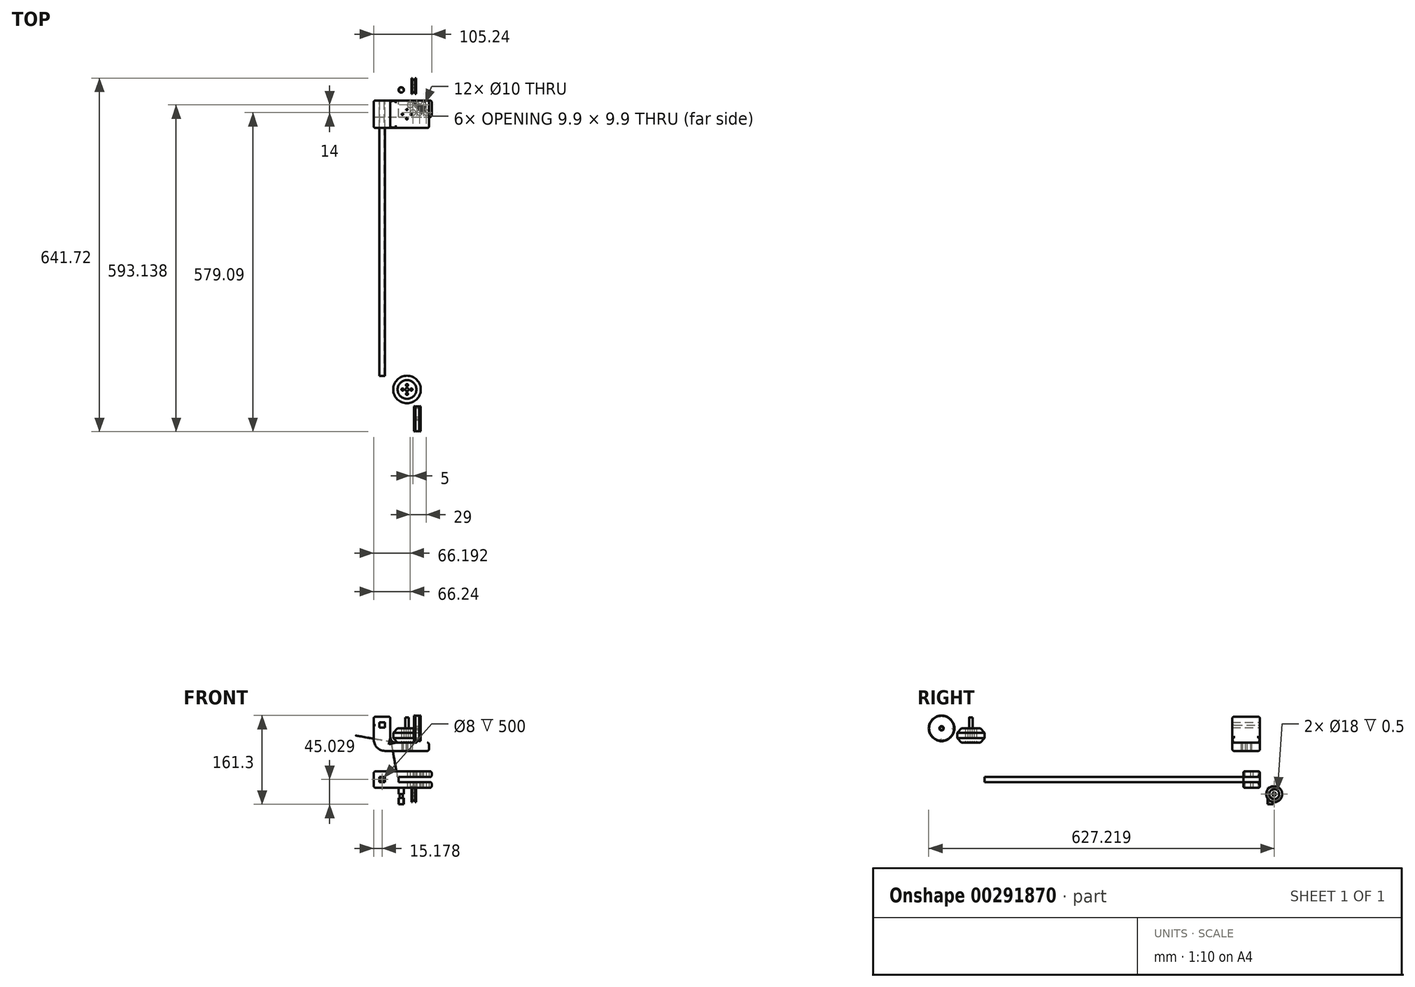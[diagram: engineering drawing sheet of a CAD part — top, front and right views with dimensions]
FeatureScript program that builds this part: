
annotation { "Feature Type Name" : "Feature", "Feature Type Description" : "" }
export const myFeature = defineFeature(function(context is Context, id is Id, definition is map)
    precondition{}
    {
        {
            var Q0;
            Q0=qCreatedBy(makeId("Front.planeOp"),FACE);
            var sketch = newSketch(context, id + "F0", { "sketchPlane" : qUnion([Q0])});
            skLineSegment(sketch, "E0.bottom", {"start": v(0, 0) * mm, "end": v(10, 0) * mm});
            skLineSegment(sketch, "E0.top", {"start": v(0, 10) * mm, "end": v(10, 10) * mm});
            skLineSegment(sketch, "E0.left", {"start": v(0, 0) * mm, "end": v(0, 10) * mm});
            skLineSegment(sketch, "E0.right", {"start": v(10, 0) * mm, "end": v(10, 10) * mm});
            skCircle(sketch, "E1", {"center": v(4.94, 5.03) * mm, "radius": 4 * mm});
            skSolve(sketch);
        }
        {
            var Q0;
            Q0=makeQuery(id+"F0.imprint","IMPRINT",FACE,{"disambiguationData":[TD([[makeQuery(id+"F0.imprint","IMPRINT",EDGE,{"derivedFrom":sQuery(id+"F0.wireOp",EDGE,"E0.bottom")}),1.0]])]});
            extrude(context, id + "F1", {"entities" : qUnion([Q0]), "depth" : 500 * mm});
        }
        {
            var Q0;
            Q0=makeQuery(id+"F0.imprint","IMPRINT",FACE,{"disambiguationData":[TD([[makeQuery(id+"F0.imprint","IMPRINT",EDGE,{"derivedFrom":sQuery(id+"F0.wireOp",EDGE,"E0.bottom")}),1.0]])]});
            var sketch = newSketch(context, id + "F2", { "sketchPlane" : qUnion([Q0])});
            skLineSegment(sketch, "E2.bottom", {"start": v(0, 0) * mm, "end": v(10, 0) * mm});
            skLineSegment(sketch, "E2.top", {"start": v(0, 10) * mm, "end": v(10, 10) * mm});
            skLineSegment(sketch, "E2.left", {"start": v(0, 0) * mm, "end": v(0, 10) * mm});
            skLineSegment(sketch, "E2.right", {"start": v(10, 0) * mm, "end": v(10, 10) * mm});
            skLineSegment(sketch, "E3.bottom", {"start": v(-10, -10) * mm, "end": v(95, -10) * mm});
            skLineSegment(sketch, "E3.top", {"start": v(-10, 20) * mm, "end": v(95, 20) * mm});
            skLineSegment(sketch, "E3.left", {"start": v(-10, -10) * mm, "end": v(-10, 20) * mm});
            skLineSegment(sketch, "E3.right", {"start": v(95, -10) * mm, "end": v(95, 20) * mm});
            skSolve(sketch);
        }
        {
            var Q0;
            Q0=makeQuery(id+"F2.imprint","IMPRINT",FACE,{"disambiguationData":[TD([[makeQuery(id+"F2.imprint","IMPRINT",EDGE,{"derivedFrom":sQuery(id+"F2.wireOp",EDGE,"E2.bottom")}),-1.0]])]});
            extrude(context, id + "F3", {"entities" : qUnion([Q0]), "depth" : 30 * mm});
        }
        {
            var Q0;
            Q0=makeQuery(id+"F3.opExtrude","SWEPT_FACE",FACE,{"disambiguationData":[OSD([sQuery(id+"F2.wireOp",EDGE,"E3.right")])]});
            var sketch = newSketch(context, id + "F4", { "sketchPlane" : qUnion([Q0])});
            skLineSegment(sketch, "E4.bottom", {"start": v(-30, 0.5) * mm, "end": v(0, 0.5) * mm});
            skLineSegment(sketch, "E4.top", {"start": v(-30, 9.5) * mm, "end": v(0, 9.5) * mm});
            skLineSegment(sketch, "E4.left", {"start": v(-30, 0.5) * mm, "end": v(-30, 9.5) * mm});
            skLineSegment(sketch, "E4.right", {"start": v(0, 0.5) * mm, "end": v(0, 9.5) * mm});
            skSolve(sketch);
        }
        {
            var Q0;
            Q0=makeQuery(id+"F4.imprint","IMPRINT",FACE,{"disambiguationData":[TD([[makeQuery(id+"F4.imprint","IMPRINT",EDGE,{"derivedFrom":sQuery(id+"F4.wireOp",EDGE,"E4.bottom")}),1.0]])]});
            extrude(context, id + "F5", {"entities" : qUnion([Q0]), "operationType" : NewBodyOperationType.REMOVE, "oppositeDirection" : true, "depth" : 60 * mm});
        }
        {
            var Q0;
            Q0=makeQuery(id+"F3.opExtrude","SWEPT_FACE",FACE,{"disambiguationData":[OSD([sQuery(id+"F2.wireOp",EDGE,"E3.bottom")])]});
            var sketch = newSketch(context, id + "F6", { "sketchPlane" : qUnion([Q0])});
            skCircle(sketch, "E5", {"center": v(85, 22) * mm, "radius": 5 * mm});
            skCircle(sketch, "E6", {"center": v(80, 8) * mm, "radius": 5 * mm});
            skCircle(sketch, "E7.1.0.0", {"center": v(73, 22) * mm, "radius": 5 * mm});
            skCircle(sketch, "E7.1.0.1", {"center": v(68, 8) * mm, "radius": 5 * mm});
            skCircle(sketch, "E7.2.0.0", {"center": v(61, 22) * mm, "radius": 5 * mm});
            skCircle(sketch, "E7.2.0.1", {"center": v(56, 8) * mm, "radius": 5 * mm});
            skCircle(sketch, "E7.3.0.0", {"center": v(49, 22) * mm, "radius": 5 * mm});
            skCircle(sketch, "E7.3.0.1", {"center": v(44, 8) * mm, "radius": 5 * mm});
            skLineSegment(sketch, "E7.direction1", {"start": v(80, 8) * mm, "end": v(68, 8) * mm, "construction": true});
            skCircle(sketch, "E8.3.0.1", {"center": v(39.68, -19.2) * mm, "radius": 2.95 * mm});
            skSolve(sketch);
        }
        {
            var Q0;
            Q0=makeQuery(id+"F3.opExtrude","CAP_EDGE",EDGE,{"disambiguationData":[OSD([sQuery(id+"F2.wireOp",EDGE,"E3.top")])],"isStart":false});
            var Q1;
            Q1=makeQuery(id+"F3.opExtrude","SWEPT_EDGE",EDGE,{"disambiguationData":[OSD([sQuery(id+"F2.wireOp",EDGE,"E3.top"),sQuery(id+"F2.wireOp",EDGE,"E3.left")])]});
            var Q2;
            Q2=makeQuery(id+"F3.opExtrude","CAP_EDGE",EDGE,{"disambiguationData":[OSD([sQuery(id+"F2.wireOp",EDGE,"E3.top")])],"isStart":true});
            var Q3;
            {var subQ0=sQuery(id+"F2.wireOp",EDGE,"E3.right");var subQ2=sQuery(id+"F2.wireOp",EDGE,"E3.top");Q3=makeQuery(id+"F5.boolean.opBoolean","SPLIT",FACE,{"disambiguationData":[TD([makeQuery(id+"F3.opExtrude","SWEPT_FACE",FACE,{"disambiguationData":[OSD([subQ2])]})])],"derivedFrom":makeQuery(id+"F3.opExtrude","SWEPT_FACE",FACE,{"disambiguationData":[OSD([subQ0])]})});}
            var Q4;
            Q4=makeQuery(id+"F3.opExtrude","SWEPT_EDGE",EDGE,{"disambiguationData":[OSD([sQuery(id+"F2.wireOp",EDGE,"E3.bottom"),sQuery(id+"F2.wireOp",EDGE,"E3.right")])]});
            var Q5;
            Q5=makeQuery(id+"F5.boolean.opBoolean","COPY",EDGE,{"derivedFrom":makeQuery(id+"F5.opExtrude","CAP_EDGE",EDGE,{"disambiguationData":[OSD([sQuery(id+"F4.wireOp",EDGE,"E4.bottom")])],"isStart":true})});
            var Q6;
            Q6=makeQuery(id+"F5.boolean.opBoolean","COPY",EDGE,{"derivedFrom":makeQuery(id+"F5.opExtrude","SWEPT_EDGE",EDGE,{"disambiguationData":[OSD([sQuery(id+"F2.wireOp",EDGE,"E3.right"),sQuery(id+"F4.wireOp",EDGE,"E4.bottom"),sQuery(id+"F4.wireOp",EDGE,"E4.left")])]})});
            var Q7;
            Q7=makeQuery(id+"F3.opExtrude","CAP_EDGE",EDGE,{"disambiguationData":[OSD([sQuery(id+"F2.wireOp",EDGE,"E3.bottom")])],"isStart":false});
            var Q8;
            Q8=makeQuery(id+"F3.opExtrude","CAP_EDGE",EDGE,{"disambiguationData":[OSD([sQuery(id+"F2.wireOp",EDGE,"E3.left")])],"isStart":false});
            var Q9;
            Q9=makeQuery(id+"F3.opExtrude","SWEPT_EDGE",EDGE,{"disambiguationData":[OSD([sQuery(id+"F2.wireOp",EDGE,"E3.bottom"),sQuery(id+"F2.wireOp",EDGE,"E3.left")])]});
            var Q10;
            Q10=makeQuery(id+"F3.opExtrude","CAP_EDGE",EDGE,{"disambiguationData":[OSD([sQuery(id+"F2.wireOp",EDGE,"E3.left")])],"isStart":true});
            var Q11;
            Q11=makeQuery(id+"F5.boolean.opBoolean","COPY",EDGE,{"derivedFrom":makeQuery(id+"F5.opExtrude","SWEPT_EDGE",EDGE,{"disambiguationData":[OSD([sQuery(id+"F2.wireOp",EDGE,"E3.right"),sQuery(id+"F4.wireOp",EDGE,"E4.bottom"),sQuery(id+"F4.wireOp",EDGE,"E4.right")])]})});
            var Q12;
            Q12=makeQuery(id+"F5.boolean.opBoolean","COPY",EDGE,{"derivedFrom":makeQuery(id+"F5.opExtrude","CAP_EDGE",EDGE,{"disambiguationData":[OSD([sQuery(id+"F4.wireOp",EDGE,"E4.right")])],"isStart":false})});
            var Q13;
            Q13=makeQuery(id+"F5.boolean.opBoolean","COPY",EDGE,{"derivedFrom":makeQuery(id+"F5.opExtrude","SWEPT_EDGE",EDGE,{"disambiguationData":[OSD([sQuery(id+"F2.wireOp",EDGE,"E3.right"),sQuery(id+"F4.wireOp",EDGE,"E4.top"),sQuery(id+"F4.wireOp",EDGE,"E4.right")])]})});
            var Q14;
            Q14=makeQuery(id+"F5.boolean.opBoolean","COPY",EDGE,{"derivedFrom":makeQuery(id+"F5.opExtrude","CAP_EDGE",EDGE,{"disambiguationData":[OSD([sQuery(id+"F4.wireOp",EDGE,"E4.left")])],"isStart":false})});
            var Q15;
            Q15=makeQuery(id+"F5.boolean.opBoolean","COPY",EDGE,{"derivedFrom":makeQuery(id+"F5.opExtrude","SWEPT_EDGE",EDGE,{"disambiguationData":[OSD([sQuery(id+"F2.wireOp",EDGE,"E3.right"),sQuery(id+"F4.wireOp",EDGE,"E4.top"),sQuery(id+"F4.wireOp",EDGE,"E4.left")])]})});
            var Q16;
            {var subQ0=sQuery(id+"F2.wireOp",EDGE,"E3.right");var subQ1=sQuery(id+"F2.wireOp",EDGE,"E3.bottom");Q16=makeQuery(id+"F5.boolean.opBoolean","SPLIT",EDGE,{"disambiguationData":[TD([makeQuery(id+"F3.opExtrude","SWEPT_FACE",FACE,{"disambiguationData":[OSD([subQ1])]})])],"derivedFrom":makeQuery(id+"F3.opExtrude","CAP_EDGE",EDGE,{"disambiguationData":[OSD([subQ0])],"isStart":false})});}
            var Q17;
            {var subQ0=sQuery(id+"F2.wireOp",EDGE,"E3.right");var subQ1=sQuery(id+"F2.wireOp",EDGE,"E3.bottom");Q17=makeQuery(id+"F5.boolean.opBoolean","SPLIT",EDGE,{"disambiguationData":[TD([makeQuery(id+"F3.opExtrude","SWEPT_FACE",FACE,{"disambiguationData":[OSD([subQ1])]})])],"derivedFrom":makeQuery(id+"F3.opExtrude","CAP_EDGE",EDGE,{"disambiguationData":[OSD([subQ0])],"isStart":true})});}
            var Q18;
            Q18=makeQuery(id+"F3.opExtrude","CAP_EDGE",EDGE,{"disambiguationData":[OSD([sQuery(id+"F2.wireOp",EDGE,"E3.bottom")])],"isStart":true});
            fillet(context, id + "F7", {"entities" : qUnion([Q0, Q1, Q2, Q3, Q4, Q5, Q6, Q7, Q8, Q9, Q10, Q11, Q12, Q13, Q14, Q15, Q16, Q17, Q18]), "radius" : 3 * mm, "tangentPropagation" : true, "allowEdgeOverflow" : false});
        }
        {
            var Q0;
            Q0=makeQuery(id+"F6.imprint","IMPRINT",FACE,{"disambiguationData":[TD([[makeQuery(id+"F6.imprint","IMPRINT",EDGE,{"derivedFrom":sQuery(id+"F6.wireOp",EDGE,"E5")}),1.0]])]});
            var Q1;
            Q1=makeQuery(id+"F6.imprint","IMPRINT",FACE,{"disambiguationData":[TD([[makeQuery(id+"F6.imprint","IMPRINT",EDGE,{"derivedFrom":sQuery(id+"F6.wireOp",EDGE,"E6")}),1.0]])]});
            var Q2;
            Q2=makeQuery(id+"F6.imprint","IMPRINT",FACE,{"disambiguationData":[TD([[makeQuery(id+"F6.imprint","IMPRINT",EDGE,{"derivedFrom":sQuery(id+"F6.wireOp",EDGE,"E7.1.0.0")}),1.0]])]});
            var Q3;
            Q3=makeQuery(id+"F6.imprint","IMPRINT",FACE,{"disambiguationData":[TD([[makeQuery(id+"F6.imprint","IMPRINT",EDGE,{"derivedFrom":sQuery(id+"F6.wireOp",EDGE,"E7.1.0.1")}),1.0]])]});
            var Q4;
            Q4=makeQuery(id+"F6.imprint","IMPRINT",FACE,{"disambiguationData":[TD([[makeQuery(id+"F6.imprint","IMPRINT",EDGE,{"derivedFrom":sQuery(id+"F6.wireOp",EDGE,"E7.2.0.0")}),1.0]])]});
            var Q5;
            Q5=makeQuery(id+"F6.imprint","IMPRINT",FACE,{"disambiguationData":[TD([[makeQuery(id+"F6.imprint","IMPRINT",EDGE,{"derivedFrom":sQuery(id+"F6.wireOp",EDGE,"E7.2.0.1")}),1.0]])]});
            var Q6;
            Q6=sQuery(id+"F6.wireOp",EDGE,"E5");
            var Q7;
            Q7=sQuery(id+"F6.wireOp",EDGE,"E6");
            var Q8;
            Q8=sQuery(id+"F6.wireOp",EDGE,"E7.1.0.1");
            var Q9;
            Q9=sQuery(id+"F6.wireOp",EDGE,"E7.1.0.0");
            var Q10;
            Q10=sQuery(id+"F6.wireOp",EDGE,"E7.2.0.0");
            extrude(context, id + "F8", {"entities" : qUnion([Q0, Q1, Q2, Q3, Q4, Q5]), "operationType" : NewBodyOperationType.REMOVE, "surfaceEntities" : qUnion([Q6, Q7, Q8, Q9, Q10]), "oppositeDirection" : true, "depth" : 30 * mm});
        }
        {
            var Q0;
            Q0=makeQuery(id+"F6.imprint","IMPRINT",FACE,{"disambiguationData":[TD([[makeQuery(id+"F6.imprint","IMPRINT",EDGE,{"derivedFrom":sQuery(id+"F6.wireOp",EDGE,"E8.3.0.1")}),1.0]])]});
            extrude(context, id + "F9", {"entities" : qUnion([Q0]), "depth" : 30 * mm});
        }
        {
            var Q0;
            Q0=makeQuery(id+"F9.opExtrude","CAP_FACE",FACE,{"disambiguationData":[OSD([sQuery(id+"F6.wireOp",EDGE,"E8.3.0.1")])],"isStart":false});
            var sketch = newSketch(context, id + "F10", { "sketchPlane" : qUnion([Q0])});
            skCircle(sketch, "E9", {"center": v(39.68, -19.2) * mm, "radius": 4.95 * mm});
            skSolve(sketch);
        }
        {
            var Q0;
            Q0=makeQuery(id+"F6.imprint","IMPRINT",FACE,{"disambiguationData":[TD([[makeQuery(id+"F6.imprint","IMPRINT",EDGE,{"derivedFrom":sQuery(id+"F6.wireOp",EDGE,"E8.3.0.1")}),1.0]])]});
            var sketch = newSketch(context, id + "F11", { "sketchPlane" : qUnion([Q0])});
            skCircle(sketch, "E10", {"center": v(39.69, -19.21) * mm, "radius": 4.9 * mm});
            skSolve(sketch);
        }
        {
            var Q0;
            Q0=makeQuery(id+"F11.imprint","IMPRINT",FACE,{"disambiguationData":[TD([[makeQuery(id+"F11.imprint","IMPRINT",EDGE,{"derivedFrom":sQuery(id+"F11.wireOp",EDGE,"E10")}),1.0]])]});
            extrude(context, id + "F12", {"entities" : qUnion([Q0]), "operationType" : NewBodyOperationType.ADD, "depth" : 11.5 * mm});
        }
        {
            var Q0;
            Q0=makeQuery(id+"F10.imprint","IMPRINT",FACE,{"disambiguationData":[TD([[makeQuery(id+"F10.imprint","IMPRINT",EDGE,{"derivedFrom":sQuery(id+"F10.wireOp",EDGE,"E9")}),1.0]])]});
            extrude(context, id + "F13", {"entities" : qUnion([Q0]), "oppositeDirection" : true, "depth" : 11.5 * mm});
        }
        {
            var Q0;
            Q0=qCreatedBy(makeId("Front.planeOp"),FACE);
            var sketch = newSketch(context, id + "F14", { "sketchPlane" : qUnion([Q0])});
            skPoint(sketch, "E11.firstSnap0", {"position": v(10, 5) * mm});
            skLineSegment(sketch, "E11.bottom", {"start": v(10, 109) * mm, "end": v(0, 109) * mm});
            skLineSegment(sketch, "E11.top", {"start": v(10, 99) * mm, "end": v(0, 99) * mm});
            skLineSegment(sketch, "E11.left", {"start": v(10, 109) * mm, "end": v(10, 99) * mm});
            skLineSegment(sketch, "E11.right", {"start": v(0, 109) * mm, "end": v(0, 104) * mm});
            skLineSegment(sketch, "E12", {"start": v(-10, 57) * mm, "end": v(90, 57) * mm});
            skLineSegment(sketch, "E13", {"start": v(90, 57) * mm, "end": v(90, 104) * mm});
            skLineSegment(sketch, "E14", {"start": v(90, 104) * mm, "end": v(-25.5, 104) * mm});
            skPoint(sketch, "E14.endSnap0", {"position": v(0, 104) * mm});
            skLineSegment(sketch, "E15", {"start": v(-10, 57) * mm, "end": v(-10, 104) * mm});
            skLineSegment(sketch, "E16", {"start": v(0, 99) * mm, "end": v(0, 104) * mm});
            skLineSegment(sketch, "E17", {"start": v(90, 72) * mm, "end": v(-10, 72) * mm});
            skLineSegment(sketch, "E18", {"start": v(20, 104) * mm, "end": v(20, 72) * mm});
            skLineSegment(sketch, "E19", {"start": v(20, 104) * mm, "end": v(20, 119) * mm});
            skLineSegment(sketch, "E20", {"start": v(20, 119) * mm, "end": v(-10.3, 119) * mm});
            skLineSegment(sketch, "E21", {"start": v(-10.3, 119) * mm, "end": v(-10, 104) * mm});
            skSolve(sketch);
        }
        {
            var Q0;
            {var subQ6=sQuery(id+"F14.wireOp",EDGE,"E11.bottom");Q0=makeQuery(id+"F14.imprint","IMPRINT",FACE,{"disambiguationData":[TD([[makeQuery(id+"F14.imprint","IMPRINT",EDGE,{"derivedFrom":subQ6}),-1.0]])]});}
            var Q1;
            {var subQ4=sQuery(id+"F14.wireOp",EDGE,"E11.top");Q1=makeQuery(id+"F14.imprint","IMPRINT",FACE,{"disambiguationData":[TD([[makeQuery(id+"F14.imprint","IMPRINT",EDGE,{"derivedFrom":subQ4}),1.0]])]});}
            var Q2;
            {var subQ1=sQuery(id+"F14.wireOp",EDGE,"E12");Q2=makeQuery(id+"F14.imprint","IMPRINT",FACE,{"disambiguationData":[TD([[makeQuery(id+"F14.imprint","IMPRINT",EDGE,{"derivedFrom":subQ1}),1.0]])]});}
            extrude(context, id + "F15", {"entities" : qUnion([Q0, Q1, Q2]), "depth" : 50 * mm});
        }
        {
            var Q0;
            Q0=makeQuery(id+"F15.opExtrude","SWEPT_EDGE",EDGE,{"disambiguationData":[OSD([sQuery(id+"F14.wireOp",EDGE,"E12"),sQuery(id+"F14.wireOp",EDGE,"E15")])]});
            fillet(context, id + "F16", {"entities" : qUnion([Q0]), "radius" : 20 * mm, "tangentPropagation" : true, "allowEdgeOverflow" : false});
        }
        {
            var Q0;
            Q0=makeQuery(id+"F15.opExtrude","SWEPT_FACE",FACE,{"disambiguationData":[OSD([sQuery(id+"F14.wireOp",EDGE,"E12")])]});
            var sketch = newSketch(context, id + "F17", { "sketchPlane" : qUnion([Q0])});
            skCircle(sketch, "E22", {"center": v(58, 25) * mm, "radius": 1.5 * mm});
            skCircle(sketch, "E23", {"center": v(42, 25) * mm, "radius": 1.5 * mm});
            skCircle(sketch, "E24", {"center": v(50, 33) * mm, "radius": 1.5 * mm});
            skCircle(sketch, "E25", {"center": v(50, 17) * mm, "radius": 1.5 * mm});
            skLineSegment(sketch, "E26", {"start": v(50, 33) * mm, "end": v(50, 17) * mm});
            skLineSegment(sketch, "E27", {"start": v(42, 25) * mm, "end": v(58, 25) * mm});
            skPoint(sketch, "E28", {"position": v(50, 25) * mm});
            skCircle(sketch, "E29", {"center": v(50, 25) * mm, "radius": 8 * mm});
            skLineSegment(sketch, "E30", {"start": v(58, 25) * mm, "end": v(42, 25) * mm});
            skLineSegment(sketch, "E31", {"start": v(50, 50) * mm, "end": v(50, 0) * mm});
            skPoint(sketch, "E31.endSnap0", {"position": v(50, 0) * mm});
            skSolve(sketch);
        }
        {
            var Q0;
            {var subQ0=sQuery(id+"F17.wireOp",EDGE,"E31");var subQ1=sQuery(id+"F17.wireOp",EDGE,"E24");var subQ2=makeQuery(id+"F17.imprint","INTERSECT",VERTEX,{"disambiguationData":[OD(0.0)],"derivedFrom":[subQ1,subQ0]});Q0=makeQuery(id+"F17.imprint","IMPRINT",FACE,{"disambiguationData":[TD([[makeQuery(id+"F17.imprint","IMPRINT",EDGE,{"disambiguationData":[TD([[subQ2,1.0]])],"derivedFrom":subQ1}),1.0]])]});}
            var Q1;
            {var subQ0=sQuery(id+"F17.wireOp",EDGE,"E31");var subQ1=sQuery(id+"F17.wireOp",EDGE,"E24");var subQ2=makeQuery(id+"F17.imprint","INTERSECT",VERTEX,{"disambiguationData":[OD(1.0)],"derivedFrom":[subQ1,subQ0]});Q1=makeQuery(id+"F17.imprint","IMPRINT",FACE,{"disambiguationData":[TD([[makeQuery(id+"F17.imprint","IMPRINT",EDGE,{"disambiguationData":[TD([[subQ2,-1.0]])],"derivedFrom":subQ1}),1.0]])]});}
            var Q2;
            {var subQ0=sQuery(id+"F17.wireOp",EDGE,"E29");var subQ1=sQuery(id+"F17.wireOp",EDGE,"E24");var subQ2=makeQuery(id+"F17.imprint","INTERSECT",VERTEX,{"disambiguationData":[OD(0.0)],"derivedFrom":[subQ1,subQ0]});Q2=makeQuery(id+"F17.imprint","IMPRINT",FACE,{"disambiguationData":[TD([[makeQuery(id+"F17.imprint","IMPRINT",EDGE,{"disambiguationData":[TD([[subQ2,-1.0]])],"derivedFrom":subQ1}),1.0]])]});}
            var Q3;
            {var subQ0=sQuery(id+"F17.wireOp",EDGE,"E29");var subQ1=sQuery(id+"F17.wireOp",EDGE,"E24");var subQ2=makeQuery(id+"F17.imprint","INTERSECT",VERTEX,{"disambiguationData":[OD(0.0)],"derivedFrom":[subQ1,subQ0]});Q3=makeQuery(id+"F17.imprint","IMPRINT",FACE,{"disambiguationData":[TD([[makeQuery(id+"F17.imprint","IMPRINT",EDGE,{"disambiguationData":[TD([[subQ2,1.0]])],"derivedFrom":subQ1}),1.0]])]});}
            var Q4;
            {var subQ0=sQuery(id+"F17.wireOp",EDGE,"E29");var subQ1=sQuery(id+"F17.wireOp",EDGE,"E23");var subQ2=makeQuery(id+"F17.imprint","INTERSECT",VERTEX,{"disambiguationData":[OD(0.0)],"derivedFrom":[subQ1,subQ0]});Q4=makeQuery(id+"F17.imprint","IMPRINT",FACE,{"disambiguationData":[TD([[makeQuery(id+"F17.imprint","IMPRINT",EDGE,{"disambiguationData":[TD([[subQ2,1.0]])],"derivedFrom":subQ1}),1.0]])]});}
            var Q5;
            {var subQ0=sQuery(id+"F17.wireOp",EDGE,"E30");var subQ1=sQuery(id+"F17.wireOp",EDGE,"E23");var subQ2=makeQuery(id+"F17.imprint","INTERSECT",VERTEX,{"derivedFrom":[subQ1,subQ0]});Q5=makeQuery(id+"F17.imprint","IMPRINT",FACE,{"disambiguationData":[TD([[makeQuery(id+"F17.imprint","IMPRINT",EDGE,{"disambiguationData":[TD([[subQ2,1.0]])],"derivedFrom":subQ1}),1.0]])]});}
            var Q6;
            {var subQ0=sQuery(id+"F17.wireOp",EDGE,"E29");var subQ1=sQuery(id+"F17.wireOp",EDGE,"E23");var subQ2=makeQuery(id+"F17.imprint","INTERSECT",VERTEX,{"disambiguationData":[OD(0.0)],"derivedFrom":[subQ1,subQ0]});Q6=makeQuery(id+"F17.imprint","IMPRINT",FACE,{"disambiguationData":[TD([[makeQuery(id+"F17.imprint","IMPRINT",EDGE,{"disambiguationData":[TD([[subQ2,-1.0]])],"derivedFrom":subQ1}),1.0]])]});}
            var Q7;
            {var subQ0=sQuery(id+"F17.wireOp",EDGE,"E29");var subQ1=sQuery(id+"F17.wireOp",EDGE,"E25");var subQ2=makeQuery(id+"F17.imprint","INTERSECT",VERTEX,{"disambiguationData":[OD(0.0)],"derivedFrom":[subQ1,subQ0]});Q7=makeQuery(id+"F17.imprint","IMPRINT",FACE,{"disambiguationData":[TD([[makeQuery(id+"F17.imprint","IMPRINT",EDGE,{"disambiguationData":[TD([[subQ2,1.0]])],"derivedFrom":subQ1}),1.0]])]});}
            var Q8;
            {var subQ0=sQuery(id+"F17.wireOp",EDGE,"E31");var subQ1=sQuery(id+"F17.wireOp",EDGE,"E25");var subQ2=makeQuery(id+"F17.imprint","INTERSECT",VERTEX,{"disambiguationData":[OD(0.0)],"derivedFrom":[subQ1,subQ0]});Q8=makeQuery(id+"F17.imprint","IMPRINT",FACE,{"disambiguationData":[TD([[makeQuery(id+"F17.imprint","IMPRINT",EDGE,{"disambiguationData":[TD([[subQ2,1.0]])],"derivedFrom":subQ1}),1.0]])]});}
            var Q9;
            {var subQ0=sQuery(id+"F17.wireOp",EDGE,"E31");var subQ1=sQuery(id+"F17.wireOp",EDGE,"E25");var subQ2=makeQuery(id+"F17.imprint","INTERSECT",VERTEX,{"disambiguationData":[OD(0.0)],"derivedFrom":[subQ1,subQ0]});Q9=makeQuery(id+"F17.imprint","IMPRINT",FACE,{"disambiguationData":[TD([[makeQuery(id+"F17.imprint","IMPRINT",EDGE,{"disambiguationData":[TD([[subQ2,-1.0]])],"derivedFrom":subQ1}),1.0]])]});}
            var Q10;
            {var subQ0=sQuery(id+"F17.wireOp",EDGE,"E29");var subQ1=sQuery(id+"F17.wireOp",EDGE,"E25");var subQ2=makeQuery(id+"F17.imprint","INTERSECT",VERTEX,{"disambiguationData":[OD(1.0)],"derivedFrom":[subQ1,subQ0]});Q10=makeQuery(id+"F17.imprint","IMPRINT",FACE,{"disambiguationData":[TD([[makeQuery(id+"F17.imprint","IMPRINT",EDGE,{"disambiguationData":[TD([[subQ2,-1.0]])],"derivedFrom":subQ1}),1.0]])]});}
            var Q11;
            {var subQ0=sQuery(id+"F17.wireOp",EDGE,"E30");var subQ1=sQuery(id+"F17.wireOp",EDGE,"E22");var subQ2=makeQuery(id+"F17.imprint","INTERSECT",VERTEX,{"derivedFrom":[subQ1,subQ0]});Q11=makeQuery(id+"F17.imprint","IMPRINT",FACE,{"disambiguationData":[TD([[makeQuery(id+"F17.imprint","IMPRINT",EDGE,{"disambiguationData":[TD([[subQ2,1.0]])],"derivedFrom":subQ1}),1.0]])]});}
            var Q12;
            {var subQ0=sQuery(id+"F17.wireOp",EDGE,"E30");var subQ1=sQuery(id+"F17.wireOp",EDGE,"E22");var subQ2=makeQuery(id+"F17.imprint","INTERSECT",VERTEX,{"derivedFrom":[subQ1,subQ0]});Q12=makeQuery(id+"F17.imprint","IMPRINT",FACE,{"disambiguationData":[TD([[makeQuery(id+"F17.imprint","IMPRINT",EDGE,{"disambiguationData":[TD([[subQ2,-1.0]])],"derivedFrom":subQ1}),1.0]])]});}
            var Q13;
            {var subQ0=sQuery(id+"F17.wireOp",EDGE,"E29");var subQ1=sQuery(id+"F17.wireOp",EDGE,"E22");var subQ2=makeQuery(id+"F17.imprint","INTERSECT",VERTEX,{"disambiguationData":[OD(0.0)],"derivedFrom":[subQ1,subQ0]});Q13=makeQuery(id+"F17.imprint","IMPRINT",FACE,{"disambiguationData":[TD([[makeQuery(id+"F17.imprint","IMPRINT",EDGE,{"disambiguationData":[TD([[subQ2,1.0]])],"derivedFrom":subQ1}),1.0]])]});}
            extrude(context, id + "F18", {"entities" : qUnion([Q0, Q1, Q2, Q3, Q4, Q5, Q6, Q7, Q8, Q9, Q10, Q11, Q12, Q13]), "operationType" : NewBodyOperationType.REMOVE, "oppositeDirection" : true, "depth" : 25 * mm});
        }
        {
            var Q0;
            Q0=makeQuery(id+"F15.opExtrude","SWEPT_FACE",FACE,{"disambiguationData":[OSD([sQuery(id+"F14.wireOp",EDGE,"E17")])]});
            var sketch = newSketch(context, id + "F19", { "sketchPlane" : qUnion([Q0])});
            skCircle(sketch, "E32", {"center": v(50.2, -524.51) * mm, "radius": 25 * mm});
            skCircle(sketch, "E33", {"center": v(50.2, -524.51) * mm, "radius": 3 * mm});
            skCircle(sketch, "E34", {"center": v(50.2, -524.51) * mm, "radius": 8 * mm});
            skCircle(sketch, "E35", {"center": v(42.2, -524.51) * mm, "radius": 2 * mm});
            skCircle(sketch, "E36.1.0", {"center": v(50.2, -516.51) * mm, "radius": 2 * mm});
            skCircle(sketch, "E36.2.0", {"center": v(58.2, -524.51) * mm, "radius": 2 * mm});
            skCircle(sketch, "E36.3.0", {"center": v(50.2, -532.51) * mm, "radius": 2 * mm});
            skLineSegment(sketch, "E36.anchor1", {"start": v(50.2, -524.51) * mm, "end": v(42.2, -524.51) * mm, "construction": true});
            skLineSegment(sketch, "E36.anchor2", {"start": v(50.2, -524.51) * mm, "end": v(50.2, -532.51) * mm, "construction": true});
            skSolve(sketch);
        }
        {
            var Q0;
            Q0=makeQuery(id+"F19.imprint","IMPRINT",FACE,{"disambiguationData":[TD([[makeQuery(id+"F19.imprint","IMPRINT",EDGE,{"derivedFrom":sQuery(id+"F19.wireOp",EDGE,"E32")}),1.0]])]});
            extrude(context, id + "F20", {"entities" : qUnion([Q0]), "depth" : 26 * mm});
        }
        {
            var Q0;
            Q0=makeQuery(id+"F20.opExtrude","CAP_EDGE",EDGE,{"disambiguationData":[OSD([sQuery(id+"F19.wireOp",EDGE,"E32")])],"isStart":false});
            var Q1;
            Q1=makeQuery(id+"F20.opExtrude","CAP_EDGE",EDGE,{"disambiguationData":[OSD([sQuery(id+"F19.wireOp",EDGE,"E32")])],"isStart":true});
            chamfer(context, id + "F21", {"entities" : qUnion([Q0, Q1]), "width" : 8 * mm, "tangentPropagation" : true});
        }
        {
            var Q0;
            Q0=makeQuery(id+"F20.opExtrude","CAP_FACE",FACE,{"disambiguationData":[OSD([sQuery(id+"F14.wireOp",EDGE,"E17"),sQuery(id+"F17.wireOp",EDGE,"E22"),sQuery(id+"F17.wireOp",EDGE,"E23"),sQuery(id+"F17.wireOp",EDGE,"E24"),sQuery(id+"F17.wireOp",EDGE,"E25"),sQuery(id+"F19.wireOp",EDGE,"E32"),sQuery(id+"F19.wireOp",EDGE,"E33")])],"isStart":false});
            var sketch = newSketch(context, id + "F22", { "sketchPlane" : qUnion([Q0])});
            skLineSegment(sketch, "E37.bottom", {"start": v(62.8, -602.8) * mm, "end": v(74.8, -602.8) * mm});
            skLineSegment(sketch, "E37.top", {"start": v(62.8, -577.8) * mm, "end": v(74.8, -577.8) * mm});
            skLineSegment(sketch, "E37.left", {"start": v(62.8, -602.8) * mm, "end": v(62.8, -577.8) * mm});
            skLineSegment(sketch, "E37.right", {"start": v(74.8, -602.8) * mm, "end": v(74.8, -577.8) * mm});
            skLineSegment(sketch, "E38", {"start": v(68.8, -602.8) * mm, "end": v(68.8, -577.8) * mm});
            skLineSegment(sketch, "E39", {"start": v(62.8, -602.8) * mm, "end": v(68.8, -596.8) * mm});
            skLineSegment(sketch, "E40", {"start": v(68.8, -596.8) * mm, "end": v(74.8, -602.8) * mm});
            skLineSegment(sketch, "E41", {"start": v(62.8, -580.8) * mm, "end": v(74.8, -580.8) * mm});
            skSolve(sketch);
        }
        {
            var Q0;
            {var subQ0=sQuery(id+"F22.wireOp",EDGE,"E39");Q0=makeQuery(id+"F22.imprint","IMPRINT",FACE,{"disambiguationData":[TD([[makeQuery(id+"F22.imprint","IMPRINT",EDGE,{"derivedFrom":subQ0}),1.0]])]});}
            var Q1;
            {var subQ0=sQuery(id+"F22.wireOp",EDGE,"E40");Q1=makeQuery(id+"F22.imprint","IMPRINT",FACE,{"disambiguationData":[TD([[makeQuery(id+"F22.imprint","IMPRINT",EDGE,{"derivedFrom":subQ0}),1.0]])]});}
            var Q2;
            Q2=sQuery(id+"F22.wireOp",EDGE,"E37.top");
            revolve(context, id + "F23", {"entities" : qUnion([Q0, Q1]), "axis" : qUnion([Q2]), "revolveType" : RevolveType.FULL});
        }
        {
            var Q0;
            Q0=makeQuery(id+"F23.opRevolve","SWEPT_EDGE",EDGE,{"disambiguationData":[OSD([sQuery(id+"F22.wireOp",EDGE,"E38"),sQuery(id+"F22.wireOp",EDGE,"E39"),sQuery(id+"F22.wireOp",EDGE,"E40")])]});
            fillet(context, id + "F24", {"entities" : qUnion([Q0]), "radius" : 1 * mm, "tangentPropagation" : true, "allowEdgeOverflow" : false});
        }
        {
            var Q0;
            Q0=makeQuery(id+"F23.opRevolve","SWEPT_EDGE",EDGE,{"disambiguationData":[OSD([sQuery(id+"F22.wireOp",EDGE,"E37.bottom"),sQuery(id+"F22.wireOp",EDGE,"E37.right"),sQuery(id+"F22.wireOp",EDGE,"E40")])]});
            var Q1;
            Q1=makeQuery(id+"F23.opRevolve","SWEPT_EDGE",EDGE,{"disambiguationData":[OSD([sQuery(id+"F22.wireOp",EDGE,"E37.bottom"),sQuery(id+"F22.wireOp",EDGE,"E37.left"),sQuery(id+"F22.wireOp",EDGE,"E39")])]});
            chamfer(context, id + "F25", {"entities" : qUnion([Q0, Q1]), "width" : 1 * mm, "tangentPropagation" : true});
        }
        {
            var Q0;
            Q0=makeQuery(id+"F23.opRevolve","SWEPT_EDGE",EDGE,{"disambiguationData":[OSD([sQuery(id+"F22.wireOp",EDGE,"E37.right"),sQuery(id+"F22.wireOp",EDGE,"E41")])]});
            var Q1;
            Q1=makeQuery(id+"F23.opRevolve","SWEPT_EDGE",EDGE,{"disambiguationData":[OSD([sQuery(id+"F22.wireOp",EDGE,"E37.left"),sQuery(id+"F22.wireOp",EDGE,"E41")])]});
            chamfer(context, id + "F26", {"entities" : qUnion([Q0, Q1]), "width" : 1 * mm, "tangentPropagation" : true});
        }
        {
            var Q0;
            Q0=makeQuery(id+"F23.opRevolve","SWEPT_FACE",FACE,{"disambiguationData":[OSD([sQuery(id+"F22.wireOp",EDGE,"E37.right")])]});
            var sketch = newSketch(context, id + "F27", { "sketchPlane" : qUnion([Q0])});
            skCircle(sketch, "E42", {"center": v(-577.8, 98) * mm, "radius": 19 * mm});
            skCircle(sketch, "E43", {"center": v(-596.79, 98.55) * mm, "radius": 0.75 * mm});
            skCircle(sketch, "E44.1.0", {"center": v(-596.64, 95.57) * mm, "radius": 0.75 * mm});
            skCircle(sketch, "E44.2.0", {"center": v(-596.03, 92.65) * mm, "radius": 0.75 * mm});
            skCircle(sketch, "E44.3.0", {"center": v(-594.96, 89.87) * mm, "radius": 0.75 * mm});
            skCircle(sketch, "E44.4.0", {"center": v(-593.48, 87.28) * mm, "radius": 0.75 * mm});
            skCircle(sketch, "E44.5.0", {"center": v(-591.6, 84.96) * mm, "radius": 0.75 * mm});
            skCircle(sketch, "E44.6.0", {"center": v(-589.4, 82.96) * mm, "radius": 0.75 * mm});
            skCircle(sketch, "E44.7.0", {"center": v(-586.9, 81.33) * mm, "radius": 0.75 * mm});
            skCircle(sketch, "E44.8.0", {"center": v(-584.18, 80.1) * mm, "radius": 0.75 * mm});
            skCircle(sketch, "E44.9.0", {"center": v(-581.3, 79.33) * mm, "radius": 0.75 * mm});
            skCircle(sketch, "E44.10.0", {"center": v(-578.34, 79.01) * mm, "radius": 0.75 * mm});
            skCircle(sketch, "E44.11.0", {"center": v(-575.36, 79.16) * mm, "radius": 0.75 * mm});
            skCircle(sketch, "E44.12.0", {"center": v(-572.44, 79.77) * mm, "radius": 0.75 * mm});
            skCircle(sketch, "E44.13.0", {"center": v(-569.66, 80.83) * mm, "radius": 0.75 * mm});
            skCircle(sketch, "E44.14.0", {"center": v(-567.07, 82.32) * mm, "radius": 0.75 * mm});
            skCircle(sketch, "E44.15.0", {"center": v(-564.75, 84.19) * mm, "radius": 0.75 * mm});
            skCircle(sketch, "E44.16.0", {"center": v(-562.75, 86.4) * mm, "radius": 0.75 * mm});
            skCircle(sketch, "E44.17.0", {"center": v(-561.12, 88.9) * mm, "radius": 0.75 * mm});
            skCircle(sketch, "E44.18.0", {"center": v(-559.9, 91.61) * mm, "radius": 0.75 * mm});
            skCircle(sketch, "E44.19.0", {"center": v(-559.12, 94.5) * mm, "radius": 0.75 * mm});
            skCircle(sketch, "E45.1.20.0", {"center": v(-558.8, 97.46) * mm, "radius": 0.75 * mm});
            skCircle(sketch, "E45.1.21.0", {"center": v(-558.95, 100.43) * mm, "radius": 0.75 * mm});
            skCircle(sketch, "E45.1.22.0", {"center": v(-559.56, 103.35) * mm, "radius": 0.75 * mm});
            skCircle(sketch, "E45.1.23.0", {"center": v(-560.62, 106.14) * mm, "radius": 0.75 * mm});
            skCircle(sketch, "E45.1.24.0", {"center": v(-562.1, 108.72) * mm, "radius": 0.75 * mm});
            skCircle(sketch, "E45.1.25.0", {"center": v(-563.98, 111.05) * mm, "radius": 0.75 * mm});
            skCircle(sketch, "E45.1.26.0", {"center": v(-566.19, 113.05) * mm, "radius": 0.75 * mm});
            skCircle(sketch, "E45.1.27.0", {"center": v(-568.68, 114.68) * mm, "radius": 0.75 * mm});
            skCircle(sketch, "E45.1.28.0", {"center": v(-571.4, 115.9) * mm, "radius": 0.75 * mm});
            skCircle(sketch, "E45.1.29.0", {"center": v(-574.28, 116.68) * mm, "radius": 0.75 * mm});
            skCircle(sketch, "E46.1.30.0", {"center": v(-577.25, 117) * mm, "radius": 0.75 * mm});
            skCircle(sketch, "E46.1.31.0", {"center": v(-580.23, 116.85) * mm, "radius": 0.75 * mm});
            skCircle(sketch, "E46.1.32.0", {"center": v(-583.14, 116.23) * mm, "radius": 0.75 * mm});
            skCircle(sketch, "E46.1.33.0", {"center": v(-585.93, 115.17) * mm, "radius": 0.75 * mm});
            skCircle(sketch, "E46.1.34.0", {"center": v(-588.52, 113.69) * mm, "radius": 0.75 * mm});
            skCircle(sketch, "E46.1.35.0", {"center": v(-590.84, 111.82) * mm, "radius": 0.75 * mm});
            skCircle(sketch, "E46.1.36.0", {"center": v(-592.84, 109.6) * mm, "radius": 0.75 * mm});
            skCircle(sketch, "E46.1.37.0", {"center": v(-594.47, 107.11) * mm, "radius": 0.75 * mm});
            skCircle(sketch, "E46.1.38.0", {"center": v(-595.69, 104.4) * mm, "radius": 0.75 * mm});
            skCircle(sketch, "E46.1.39.0", {"center": v(-596.47, 101.51) * mm, "radius": 0.75 * mm});
            skSolve(sketch);
        }
        {
            var Q0;
            {var subQ0=sQuery(id+"F27.wireOp",EDGE,"E45.1.21.0");var subQ1=sQuery(id+"F27.wireOp",EDGE,"E42");var subQ2=makeQuery(id+"F27.imprint","INTERSECT",VERTEX,{"disambiguationData":[OD(0.0)],"derivedFrom":[subQ1,subQ0]});Q0=makeQuery(id+"F27.imprint","IMPRINT",FACE,{"disambiguationData":[TD([[makeQuery(id+"F27.imprint","IMPRINT",EDGE,{"disambiguationData":[TD([[subQ2,-1.0]])],"derivedFrom":subQ1}),-1.0]])]});}
            var Q1;
            {var subQ0=sQuery(id+"F27.wireOp",EDGE,"E45.1.21.0");var subQ1=sQuery(id+"F27.wireOp",EDGE,"E42");var subQ2=makeQuery(id+"F27.imprint","INTERSECT",VERTEX,{"disambiguationData":[OD(0.0)],"derivedFrom":[subQ1,subQ0]});Q1=makeQuery(id+"F27.imprint","IMPRINT",FACE,{"disambiguationData":[TD([[makeQuery(id+"F27.imprint","IMPRINT",EDGE,{"disambiguationData":[TD([[subQ2,-1.0]])],"derivedFrom":subQ1}),1.0]])]});}
            var Q2;
            {var subQ0=sQuery(id+"F27.wireOp",EDGE,"E45.1.22.0");var subQ1=sQuery(id+"F27.wireOp",EDGE,"E42");var subQ2=makeQuery(id+"F27.imprint","INTERSECT",VERTEX,{"disambiguationData":[OD(0.0)],"derivedFrom":[subQ1,subQ0]});Q2=makeQuery(id+"F27.imprint","IMPRINT",FACE,{"disambiguationData":[TD([[makeQuery(id+"F27.imprint","IMPRINT",EDGE,{"disambiguationData":[TD([[subQ2,-1.0]])],"derivedFrom":subQ1}),-1.0]])]});}
            var Q3;
            {var subQ0=sQuery(id+"F27.wireOp",EDGE,"E45.1.22.0");var subQ1=sQuery(id+"F27.wireOp",EDGE,"E42");var subQ2=makeQuery(id+"F27.imprint","INTERSECT",VERTEX,{"disambiguationData":[OD(0.0)],"derivedFrom":[subQ1,subQ0]});Q3=makeQuery(id+"F27.imprint","IMPRINT",FACE,{"disambiguationData":[TD([[makeQuery(id+"F27.imprint","IMPRINT",EDGE,{"disambiguationData":[TD([[subQ2,-1.0]])],"derivedFrom":subQ1}),1.0]])]});}
            var Q4;
            {var subQ0=sQuery(id+"F27.wireOp",EDGE,"E45.1.23.0");var subQ1=sQuery(id+"F27.wireOp",EDGE,"E42");var subQ2=makeQuery(id+"F27.imprint","INTERSECT",VERTEX,{"disambiguationData":[OD(0.0)],"derivedFrom":[subQ1,subQ0]});Q4=makeQuery(id+"F27.imprint","IMPRINT",FACE,{"disambiguationData":[TD([[makeQuery(id+"F27.imprint","IMPRINT",EDGE,{"disambiguationData":[TD([[subQ2,-1.0]])],"derivedFrom":subQ1}),-1.0]])]});}
            var Q5;
            {var subQ0=sQuery(id+"F27.wireOp",EDGE,"E45.1.23.0");var subQ1=sQuery(id+"F27.wireOp",EDGE,"E42");var subQ2=makeQuery(id+"F27.imprint","INTERSECT",VERTEX,{"disambiguationData":[OD(0.0)],"derivedFrom":[subQ1,subQ0]});Q5=makeQuery(id+"F27.imprint","IMPRINT",FACE,{"disambiguationData":[TD([[makeQuery(id+"F27.imprint","IMPRINT",EDGE,{"disambiguationData":[TD([[subQ2,-1.0]])],"derivedFrom":subQ1}),1.0]])]});}
            var Q6;
            {var subQ0=sQuery(id+"F27.wireOp",EDGE,"E45.1.24.0");var subQ1=sQuery(id+"F27.wireOp",EDGE,"E42");var subQ2=makeQuery(id+"F27.imprint","INTERSECT",VERTEX,{"disambiguationData":[OD(0.0)],"derivedFrom":[subQ1,subQ0]});Q6=makeQuery(id+"F27.imprint","IMPRINT",FACE,{"disambiguationData":[TD([[makeQuery(id+"F27.imprint","IMPRINT",EDGE,{"disambiguationData":[TD([[subQ2,-1.0]])],"derivedFrom":subQ1}),-1.0]])]});}
            var Q7;
            {var subQ0=sQuery(id+"F27.wireOp",EDGE,"E45.1.24.0");var subQ1=sQuery(id+"F27.wireOp",EDGE,"E42");var subQ2=makeQuery(id+"F27.imprint","INTERSECT",VERTEX,{"disambiguationData":[OD(0.0)],"derivedFrom":[subQ1,subQ0]});Q7=makeQuery(id+"F27.imprint","IMPRINT",FACE,{"disambiguationData":[TD([[makeQuery(id+"F27.imprint","IMPRINT",EDGE,{"disambiguationData":[TD([[subQ2,-1.0]])],"derivedFrom":subQ1}),1.0]])]});}
            var Q8;
            {var subQ0=sQuery(id+"F27.wireOp",EDGE,"E45.1.25.0");var subQ1=sQuery(id+"F27.wireOp",EDGE,"E42");var subQ2=makeQuery(id+"F27.imprint","INTERSECT",VERTEX,{"disambiguationData":[OD(0.0)],"derivedFrom":[subQ1,subQ0]});Q8=makeQuery(id+"F27.imprint","IMPRINT",FACE,{"disambiguationData":[TD([[makeQuery(id+"F27.imprint","IMPRINT",EDGE,{"disambiguationData":[TD([[subQ2,-1.0]])],"derivedFrom":subQ1}),-1.0]])]});}
            var Q9;
            {var subQ0=sQuery(id+"F27.wireOp",EDGE,"E45.1.25.0");var subQ1=sQuery(id+"F27.wireOp",EDGE,"E42");var subQ2=makeQuery(id+"F27.imprint","INTERSECT",VERTEX,{"disambiguationData":[OD(0.0)],"derivedFrom":[subQ1,subQ0]});Q9=makeQuery(id+"F27.imprint","IMPRINT",FACE,{"disambiguationData":[TD([[makeQuery(id+"F27.imprint","IMPRINT",EDGE,{"disambiguationData":[TD([[subQ2,-1.0]])],"derivedFrom":subQ1}),1.0]])]});}
            var Q10;
            {var subQ0=sQuery(id+"F27.wireOp",EDGE,"E45.1.26.0");var subQ1=sQuery(id+"F27.wireOp",EDGE,"E42");var subQ2=makeQuery(id+"F27.imprint","INTERSECT",VERTEX,{"disambiguationData":[OD(0.0)],"derivedFrom":[subQ1,subQ0]});Q10=makeQuery(id+"F27.imprint","IMPRINT",FACE,{"disambiguationData":[TD([[makeQuery(id+"F27.imprint","IMPRINT",EDGE,{"disambiguationData":[TD([[subQ2,-1.0]])],"derivedFrom":subQ1}),-1.0]])]});}
            var Q11;
            {var subQ0=sQuery(id+"F27.wireOp",EDGE,"E45.1.26.0");var subQ1=sQuery(id+"F27.wireOp",EDGE,"E42");var subQ2=makeQuery(id+"F27.imprint","INTERSECT",VERTEX,{"disambiguationData":[OD(0.0)],"derivedFrom":[subQ1,subQ0]});Q11=makeQuery(id+"F27.imprint","IMPRINT",FACE,{"disambiguationData":[TD([[makeQuery(id+"F27.imprint","IMPRINT",EDGE,{"disambiguationData":[TD([[subQ2,-1.0]])],"derivedFrom":subQ1}),1.0]])]});}
            var Q12;
            {var subQ0=sQuery(id+"F27.wireOp",EDGE,"E45.1.27.0");var subQ1=sQuery(id+"F27.wireOp",EDGE,"E42");var subQ2=makeQuery(id+"F27.imprint","INTERSECT",VERTEX,{"disambiguationData":[OD(0.0)],"derivedFrom":[subQ1,subQ0]});Q12=makeQuery(id+"F27.imprint","IMPRINT",FACE,{"disambiguationData":[TD([[makeQuery(id+"F27.imprint","IMPRINT",EDGE,{"disambiguationData":[TD([[subQ2,-1.0]])],"derivedFrom":subQ1}),-1.0]])]});}
            var Q13;
            {var subQ0=sQuery(id+"F27.wireOp",EDGE,"E45.1.27.0");var subQ1=sQuery(id+"F27.wireOp",EDGE,"E42");var subQ2=makeQuery(id+"F27.imprint","INTERSECT",VERTEX,{"disambiguationData":[OD(0.0)],"derivedFrom":[subQ1,subQ0]});Q13=makeQuery(id+"F27.imprint","IMPRINT",FACE,{"disambiguationData":[TD([[makeQuery(id+"F27.imprint","IMPRINT",EDGE,{"disambiguationData":[TD([[subQ2,-1.0]])],"derivedFrom":subQ1}),1.0]])]});}
            var Q14;
            {var subQ0=sQuery(id+"F27.wireOp",EDGE,"E45.1.28.0");var subQ1=sQuery(id+"F27.wireOp",EDGE,"E42");var subQ2=makeQuery(id+"F27.imprint","INTERSECT",VERTEX,{"disambiguationData":[OD(0.0)],"derivedFrom":[subQ1,subQ0]});Q14=makeQuery(id+"F27.imprint","IMPRINT",FACE,{"disambiguationData":[TD([[makeQuery(id+"F27.imprint","IMPRINT",EDGE,{"disambiguationData":[TD([[subQ2,-1.0]])],"derivedFrom":subQ1}),-1.0]])]});}
            var Q15;
            {var subQ0=sQuery(id+"F27.wireOp",EDGE,"E45.1.28.0");var subQ1=sQuery(id+"F27.wireOp",EDGE,"E42");var subQ2=makeQuery(id+"F27.imprint","INTERSECT",VERTEX,{"disambiguationData":[OD(0.0)],"derivedFrom":[subQ1,subQ0]});Q15=makeQuery(id+"F27.imprint","IMPRINT",FACE,{"disambiguationData":[TD([[makeQuery(id+"F27.imprint","IMPRINT",EDGE,{"disambiguationData":[TD([[subQ2,-1.0]])],"derivedFrom":subQ1}),1.0]])]});}
            var Q16;
            {var subQ0=sQuery(id+"F27.wireOp",EDGE,"E45.1.29.0");var subQ1=sQuery(id+"F27.wireOp",EDGE,"E42");var subQ2=makeQuery(id+"F27.imprint","INTERSECT",VERTEX,{"disambiguationData":[OD(0.0)],"derivedFrom":[subQ1,subQ0]});Q16=makeQuery(id+"F27.imprint","IMPRINT",FACE,{"disambiguationData":[TD([[makeQuery(id+"F27.imprint","IMPRINT",EDGE,{"disambiguationData":[TD([[subQ2,-1.0]])],"derivedFrom":subQ1}),-1.0]])]});}
            var Q17;
            {var subQ0=sQuery(id+"F27.wireOp",EDGE,"E45.1.29.0");var subQ1=sQuery(id+"F27.wireOp",EDGE,"E42");var subQ2=makeQuery(id+"F27.imprint","INTERSECT",VERTEX,{"disambiguationData":[OD(0.0)],"derivedFrom":[subQ1,subQ0]});Q17=makeQuery(id+"F27.imprint","IMPRINT",FACE,{"disambiguationData":[TD([[makeQuery(id+"F27.imprint","IMPRINT",EDGE,{"disambiguationData":[TD([[subQ2,-1.0]])],"derivedFrom":subQ1}),1.0]])]});}
            var Q18;
            {var subQ0=sQuery(id+"F27.wireOp",EDGE,"E46.1.30.0");var subQ1=sQuery(id+"F27.wireOp",EDGE,"E42");var subQ2=makeQuery(id+"F27.imprint","INTERSECT",VERTEX,{"disambiguationData":[OD(0.0)],"derivedFrom":[subQ1,subQ0]});Q18=makeQuery(id+"F27.imprint","IMPRINT",FACE,{"disambiguationData":[TD([[makeQuery(id+"F27.imprint","IMPRINT",EDGE,{"disambiguationData":[TD([[subQ2,-1.0]])],"derivedFrom":subQ1}),-1.0]])]});}
            var Q19;
            {var subQ0=sQuery(id+"F27.wireOp",EDGE,"E46.1.30.0");var subQ1=sQuery(id+"F27.wireOp",EDGE,"E42");var subQ2=makeQuery(id+"F27.imprint","INTERSECT",VERTEX,{"disambiguationData":[OD(0.0)],"derivedFrom":[subQ1,subQ0]});Q19=makeQuery(id+"F27.imprint","IMPRINT",FACE,{"disambiguationData":[TD([[makeQuery(id+"F27.imprint","IMPRINT",EDGE,{"disambiguationData":[TD([[subQ2,-1.0]])],"derivedFrom":subQ1}),1.0]])]});}
            var Q20;
            {var subQ0=sQuery(id+"F27.wireOp",EDGE,"E46.1.31.0");var subQ1=sQuery(id+"F27.wireOp",EDGE,"E42");var subQ2=makeQuery(id+"F27.imprint","INTERSECT",VERTEX,{"disambiguationData":[OD(0.0)],"derivedFrom":[subQ1,subQ0]});Q20=makeQuery(id+"F27.imprint","IMPRINT",FACE,{"disambiguationData":[TD([[makeQuery(id+"F27.imprint","IMPRINT",EDGE,{"disambiguationData":[TD([[subQ2,-1.0]])],"derivedFrom":subQ1}),-1.0]])]});}
            var Q21;
            {var subQ0=sQuery(id+"F27.wireOp",EDGE,"E46.1.31.0");var subQ1=sQuery(id+"F27.wireOp",EDGE,"E42");var subQ2=makeQuery(id+"F27.imprint","INTERSECT",VERTEX,{"disambiguationData":[OD(0.0)],"derivedFrom":[subQ1,subQ0]});Q21=makeQuery(id+"F27.imprint","IMPRINT",FACE,{"disambiguationData":[TD([[makeQuery(id+"F27.imprint","IMPRINT",EDGE,{"disambiguationData":[TD([[subQ2,-1.0]])],"derivedFrom":subQ1}),1.0]])]});}
            var Q22;
            {var subQ0=sQuery(id+"F27.wireOp",EDGE,"E46.1.32.0");var subQ1=sQuery(id+"F27.wireOp",EDGE,"E42");var subQ2=makeQuery(id+"F27.imprint","INTERSECT",VERTEX,{"disambiguationData":[OD(0.0)],"derivedFrom":[subQ1,subQ0]});Q22=makeQuery(id+"F27.imprint","IMPRINT",FACE,{"disambiguationData":[TD([[makeQuery(id+"F27.imprint","IMPRINT",EDGE,{"disambiguationData":[TD([[subQ2,-1.0]])],"derivedFrom":subQ1}),-1.0]])]});}
            var Q23;
            {var subQ0=sQuery(id+"F27.wireOp",EDGE,"E46.1.32.0");var subQ1=sQuery(id+"F27.wireOp",EDGE,"E42");var subQ2=makeQuery(id+"F27.imprint","INTERSECT",VERTEX,{"disambiguationData":[OD(0.0)],"derivedFrom":[subQ1,subQ0]});Q23=makeQuery(id+"F27.imprint","IMPRINT",FACE,{"disambiguationData":[TD([[makeQuery(id+"F27.imprint","IMPRINT",EDGE,{"disambiguationData":[TD([[subQ2,-1.0]])],"derivedFrom":subQ1}),1.0]])]});}
            var Q24;
            {var subQ0=sQuery(id+"F27.wireOp",EDGE,"E46.1.33.0");var subQ1=sQuery(id+"F27.wireOp",EDGE,"E42");var subQ2=makeQuery(id+"F27.imprint","INTERSECT",VERTEX,{"disambiguationData":[OD(0.0)],"derivedFrom":[subQ1,subQ0]});Q24=makeQuery(id+"F27.imprint","IMPRINT",FACE,{"disambiguationData":[TD([[makeQuery(id+"F27.imprint","IMPRINT",EDGE,{"disambiguationData":[TD([[subQ2,-1.0]])],"derivedFrom":subQ1}),-1.0]])]});}
            var Q25;
            {var subQ0=sQuery(id+"F27.wireOp",EDGE,"E46.1.33.0");var subQ1=sQuery(id+"F27.wireOp",EDGE,"E42");var subQ2=makeQuery(id+"F27.imprint","INTERSECT",VERTEX,{"disambiguationData":[OD(0.0)],"derivedFrom":[subQ1,subQ0]});Q25=makeQuery(id+"F27.imprint","IMPRINT",FACE,{"disambiguationData":[TD([[makeQuery(id+"F27.imprint","IMPRINT",EDGE,{"disambiguationData":[TD([[subQ2,-1.0]])],"derivedFrom":subQ1}),1.0]])]});}
            var Q26;
            {var subQ0=sQuery(id+"F27.wireOp",EDGE,"E46.1.34.0");var subQ1=sQuery(id+"F27.wireOp",EDGE,"E42");var subQ2=makeQuery(id+"F27.imprint","INTERSECT",VERTEX,{"disambiguationData":[OD(0.0)],"derivedFrom":[subQ1,subQ0]});Q26=makeQuery(id+"F27.imprint","IMPRINT",FACE,{"disambiguationData":[TD([[makeQuery(id+"F27.imprint","IMPRINT",EDGE,{"disambiguationData":[TD([[subQ2,-1.0]])],"derivedFrom":subQ1}),-1.0]])]});}
            var Q27;
            {var subQ0=sQuery(id+"F27.wireOp",EDGE,"E46.1.34.0");var subQ1=sQuery(id+"F27.wireOp",EDGE,"E42");var subQ2=makeQuery(id+"F27.imprint","INTERSECT",VERTEX,{"disambiguationData":[OD(0.0)],"derivedFrom":[subQ1,subQ0]});Q27=makeQuery(id+"F27.imprint","IMPRINT",FACE,{"disambiguationData":[TD([[makeQuery(id+"F27.imprint","IMPRINT",EDGE,{"disambiguationData":[TD([[subQ2,-1.0]])],"derivedFrom":subQ1}),1.0]])]});}
            var Q28;
            {var subQ0=sQuery(id+"F27.wireOp",EDGE,"E46.1.35.0");var subQ1=sQuery(id+"F27.wireOp",EDGE,"E42");var subQ2=makeQuery(id+"F27.imprint","INTERSECT",VERTEX,{"disambiguationData":[OD(0.0)],"derivedFrom":[subQ1,subQ0]});Q28=makeQuery(id+"F27.imprint","IMPRINT",FACE,{"disambiguationData":[TD([[makeQuery(id+"F27.imprint","IMPRINT",EDGE,{"disambiguationData":[TD([[subQ2,-1.0]])],"derivedFrom":subQ1}),-1.0]])]});}
            var Q29;
            {var subQ0=sQuery(id+"F27.wireOp",EDGE,"E46.1.35.0");var subQ1=sQuery(id+"F27.wireOp",EDGE,"E42");var subQ2=makeQuery(id+"F27.imprint","INTERSECT",VERTEX,{"disambiguationData":[OD(0.0)],"derivedFrom":[subQ1,subQ0]});Q29=makeQuery(id+"F27.imprint","IMPRINT",FACE,{"disambiguationData":[TD([[makeQuery(id+"F27.imprint","IMPRINT",EDGE,{"disambiguationData":[TD([[subQ2,-1.0]])],"derivedFrom":subQ1}),1.0]])]});}
            var Q30;
            {var subQ0=sQuery(id+"F27.wireOp",EDGE,"E46.1.36.0");var subQ1=sQuery(id+"F27.wireOp",EDGE,"E42");var subQ2=makeQuery(id+"F27.imprint","INTERSECT",VERTEX,{"disambiguationData":[OD(0.0)],"derivedFrom":[subQ1,subQ0]});Q30=makeQuery(id+"F27.imprint","IMPRINT",FACE,{"disambiguationData":[TD([[makeQuery(id+"F27.imprint","IMPRINT",EDGE,{"disambiguationData":[TD([[subQ2,-1.0]])],"derivedFrom":subQ1}),-1.0]])]});}
            var Q31;
            {var subQ0=sQuery(id+"F27.wireOp",EDGE,"E46.1.36.0");var subQ1=sQuery(id+"F27.wireOp",EDGE,"E42");var subQ2=makeQuery(id+"F27.imprint","INTERSECT",VERTEX,{"disambiguationData":[OD(0.0)],"derivedFrom":[subQ1,subQ0]});Q31=makeQuery(id+"F27.imprint","IMPRINT",FACE,{"disambiguationData":[TD([[makeQuery(id+"F27.imprint","IMPRINT",EDGE,{"disambiguationData":[TD([[subQ2,-1.0]])],"derivedFrom":subQ1}),1.0]])]});}
            var Q32;
            {var subQ0=sQuery(id+"F27.wireOp",EDGE,"E46.1.37.0");var subQ1=sQuery(id+"F27.wireOp",EDGE,"E42");var subQ2=makeQuery(id+"F27.imprint","INTERSECT",VERTEX,{"disambiguationData":[OD(0.0)],"derivedFrom":[subQ1,subQ0]});Q32=makeQuery(id+"F27.imprint","IMPRINT",FACE,{"disambiguationData":[TD([[makeQuery(id+"F27.imprint","IMPRINT",EDGE,{"disambiguationData":[TD([[subQ2,-1.0]])],"derivedFrom":subQ1}),-1.0]])]});}
            var Q33;
            {var subQ0=sQuery(id+"F27.wireOp",EDGE,"E46.1.37.0");var subQ1=sQuery(id+"F27.wireOp",EDGE,"E42");var subQ2=makeQuery(id+"F27.imprint","INTERSECT",VERTEX,{"disambiguationData":[OD(0.0)],"derivedFrom":[subQ1,subQ0]});Q33=makeQuery(id+"F27.imprint","IMPRINT",FACE,{"disambiguationData":[TD([[makeQuery(id+"F27.imprint","IMPRINT",EDGE,{"disambiguationData":[TD([[subQ2,-1.0]])],"derivedFrom":subQ1}),1.0]])]});}
            var Q34;
            {var subQ0=sQuery(id+"F27.wireOp",EDGE,"E46.1.38.0");var subQ1=sQuery(id+"F27.wireOp",EDGE,"E42");var subQ2=makeQuery(id+"F27.imprint","INTERSECT",VERTEX,{"disambiguationData":[OD(0.0)],"derivedFrom":[subQ1,subQ0]});Q34=makeQuery(id+"F27.imprint","IMPRINT",FACE,{"disambiguationData":[TD([[makeQuery(id+"F27.imprint","IMPRINT",EDGE,{"disambiguationData":[TD([[subQ2,-1.0]])],"derivedFrom":subQ1}),-1.0]])]});}
            var Q35;
            {var subQ0=sQuery(id+"F27.wireOp",EDGE,"E46.1.38.0");var subQ1=sQuery(id+"F27.wireOp",EDGE,"E42");var subQ2=makeQuery(id+"F27.imprint","INTERSECT",VERTEX,{"disambiguationData":[OD(0.0)],"derivedFrom":[subQ1,subQ0]});Q35=makeQuery(id+"F27.imprint","IMPRINT",FACE,{"disambiguationData":[TD([[makeQuery(id+"F27.imprint","IMPRINT",EDGE,{"disambiguationData":[TD([[subQ2,-1.0]])],"derivedFrom":subQ1}),1.0]])]});}
            var Q36;
            {var subQ0=sQuery(id+"F27.wireOp",EDGE,"E46.1.39.0");var subQ1=sQuery(id+"F27.wireOp",EDGE,"E42");var subQ2=makeQuery(id+"F27.imprint","INTERSECT",VERTEX,{"disambiguationData":[OD(0.0)],"derivedFrom":[subQ1,subQ0]});Q36=makeQuery(id+"F27.imprint","IMPRINT",FACE,{"disambiguationData":[TD([[makeQuery(id+"F27.imprint","IMPRINT",EDGE,{"disambiguationData":[TD([[subQ2,-1.0]])],"derivedFrom":subQ1}),-1.0]])]});}
            var Q37;
            {var subQ0=sQuery(id+"F27.wireOp",EDGE,"E46.1.39.0");var subQ1=sQuery(id+"F27.wireOp",EDGE,"E42");var subQ2=makeQuery(id+"F27.imprint","INTERSECT",VERTEX,{"disambiguationData":[OD(0.0)],"derivedFrom":[subQ1,subQ0]});Q37=makeQuery(id+"F27.imprint","IMPRINT",FACE,{"disambiguationData":[TD([[makeQuery(id+"F27.imprint","IMPRINT",EDGE,{"disambiguationData":[TD([[subQ2,-1.0]])],"derivedFrom":subQ1}),1.0]])]});}
            var Q38;
            {var subQ0=sQuery(id+"F27.wireOp",EDGE,"E43");var subQ1=sQuery(id+"F27.wireOp",EDGE,"E42");var subQ2=makeQuery(id+"F27.imprint","INTERSECT",VERTEX,{"disambiguationData":[OD(0.0)],"derivedFrom":[subQ1,subQ0]});Q38=makeQuery(id+"F27.imprint","IMPRINT",FACE,{"disambiguationData":[TD([[makeQuery(id+"F27.imprint","IMPRINT",EDGE,{"disambiguationData":[TD([[subQ2,-1.0]])],"derivedFrom":subQ1}),-1.0]])]});}
            var Q39;
            {var subQ0=sQuery(id+"F27.wireOp",EDGE,"E43");var subQ1=sQuery(id+"F27.wireOp",EDGE,"E42");var subQ2=makeQuery(id+"F27.imprint","INTERSECT",VERTEX,{"disambiguationData":[OD(0.0)],"derivedFrom":[subQ1,subQ0]});Q39=makeQuery(id+"F27.imprint","IMPRINT",FACE,{"disambiguationData":[TD([[makeQuery(id+"F27.imprint","IMPRINT",EDGE,{"disambiguationData":[TD([[subQ2,-1.0]])],"derivedFrom":subQ1}),1.0]])]});}
            var Q40;
            {var subQ0=sQuery(id+"F27.wireOp",EDGE,"E44.1.0");var subQ1=sQuery(id+"F27.wireOp",EDGE,"E42");var subQ2=makeQuery(id+"F27.imprint","INTERSECT",VERTEX,{"disambiguationData":[OD(0.0)],"derivedFrom":[subQ1,subQ0]});Q40=makeQuery(id+"F27.imprint","IMPRINT",FACE,{"disambiguationData":[TD([[makeQuery(id+"F27.imprint","IMPRINT",EDGE,{"disambiguationData":[TD([[subQ2,-1.0]])],"derivedFrom":subQ1}),-1.0]])]});}
            var Q41;
            {var subQ0=sQuery(id+"F27.wireOp",EDGE,"E44.1.0");var subQ1=sQuery(id+"F27.wireOp",EDGE,"E42");var subQ2=makeQuery(id+"F27.imprint","INTERSECT",VERTEX,{"disambiguationData":[OD(0.0)],"derivedFrom":[subQ1,subQ0]});Q41=makeQuery(id+"F27.imprint","IMPRINT",FACE,{"disambiguationData":[TD([[makeQuery(id+"F27.imprint","IMPRINT",EDGE,{"disambiguationData":[TD([[subQ2,-1.0]])],"derivedFrom":subQ1}),1.0]])]});}
            var Q42;
            {var subQ0=sQuery(id+"F27.wireOp",EDGE,"E44.2.0");var subQ1=sQuery(id+"F27.wireOp",EDGE,"E42");var subQ2=makeQuery(id+"F27.imprint","INTERSECT",VERTEX,{"disambiguationData":[OD(0.0)],"derivedFrom":[subQ1,subQ0]});Q42=makeQuery(id+"F27.imprint","IMPRINT",FACE,{"disambiguationData":[TD([[makeQuery(id+"F27.imprint","IMPRINT",EDGE,{"disambiguationData":[TD([[subQ2,-1.0]])],"derivedFrom":subQ1}),-1.0]])]});}
            var Q43;
            {var subQ0=sQuery(id+"F27.wireOp",EDGE,"E44.2.0");var subQ1=sQuery(id+"F27.wireOp",EDGE,"E42");var subQ2=makeQuery(id+"F27.imprint","INTERSECT",VERTEX,{"disambiguationData":[OD(0.0)],"derivedFrom":[subQ1,subQ0]});Q43=makeQuery(id+"F27.imprint","IMPRINT",FACE,{"disambiguationData":[TD([[makeQuery(id+"F27.imprint","IMPRINT",EDGE,{"disambiguationData":[TD([[subQ2,-1.0]])],"derivedFrom":subQ1}),1.0]])]});}
            var Q44;
            {var subQ0=sQuery(id+"F27.wireOp",EDGE,"E44.3.0");var subQ1=sQuery(id+"F27.wireOp",EDGE,"E42");var subQ2=makeQuery(id+"F27.imprint","INTERSECT",VERTEX,{"disambiguationData":[OD(0.0)],"derivedFrom":[subQ1,subQ0]});Q44=makeQuery(id+"F27.imprint","IMPRINT",FACE,{"disambiguationData":[TD([[makeQuery(id+"F27.imprint","IMPRINT",EDGE,{"disambiguationData":[TD([[subQ2,-1.0]])],"derivedFrom":subQ1}),-1.0]])]});}
            var Q45;
            {var subQ0=sQuery(id+"F27.wireOp",EDGE,"E44.3.0");var subQ1=sQuery(id+"F27.wireOp",EDGE,"E42");var subQ2=makeQuery(id+"F27.imprint","INTERSECT",VERTEX,{"disambiguationData":[OD(0.0)],"derivedFrom":[subQ1,subQ0]});Q45=makeQuery(id+"F27.imprint","IMPRINT",FACE,{"disambiguationData":[TD([[makeQuery(id+"F27.imprint","IMPRINT",EDGE,{"disambiguationData":[TD([[subQ2,-1.0]])],"derivedFrom":subQ1}),1.0]])]});}
            var Q46;
            {var subQ0=sQuery(id+"F27.wireOp",EDGE,"E44.4.0");var subQ1=sQuery(id+"F27.wireOp",EDGE,"E42");var subQ2=makeQuery(id+"F27.imprint","INTERSECT",VERTEX,{"disambiguationData":[OD(0.0)],"derivedFrom":[subQ1,subQ0]});Q46=makeQuery(id+"F27.imprint","IMPRINT",FACE,{"disambiguationData":[TD([[makeQuery(id+"F27.imprint","IMPRINT",EDGE,{"disambiguationData":[TD([[subQ2,-1.0]])],"derivedFrom":subQ1}),-1.0]])]});}
            var Q47;
            {var subQ0=sQuery(id+"F27.wireOp",EDGE,"E44.4.0");var subQ1=sQuery(id+"F27.wireOp",EDGE,"E42");var subQ2=makeQuery(id+"F27.imprint","INTERSECT",VERTEX,{"disambiguationData":[OD(0.0)],"derivedFrom":[subQ1,subQ0]});Q47=makeQuery(id+"F27.imprint","IMPRINT",FACE,{"disambiguationData":[TD([[makeQuery(id+"F27.imprint","IMPRINT",EDGE,{"disambiguationData":[TD([[subQ2,-1.0]])],"derivedFrom":subQ1}),1.0]])]});}
            var Q48;
            {var subQ0=sQuery(id+"F27.wireOp",EDGE,"E44.5.0");var subQ1=sQuery(id+"F27.wireOp",EDGE,"E42");var subQ2=makeQuery(id+"F27.imprint","INTERSECT",VERTEX,{"disambiguationData":[OD(0.0)],"derivedFrom":[subQ1,subQ0]});Q48=makeQuery(id+"F27.imprint","IMPRINT",FACE,{"disambiguationData":[TD([[makeQuery(id+"F27.imprint","IMPRINT",EDGE,{"disambiguationData":[TD([[subQ2,-1.0]])],"derivedFrom":subQ1}),-1.0]])]});}
            var Q49;
            {var subQ0=sQuery(id+"F27.wireOp",EDGE,"E44.5.0");var subQ1=sQuery(id+"F27.wireOp",EDGE,"E42");var subQ2=makeQuery(id+"F27.imprint","INTERSECT",VERTEX,{"disambiguationData":[OD(0.0)],"derivedFrom":[subQ1,subQ0]});Q49=makeQuery(id+"F27.imprint","IMPRINT",FACE,{"disambiguationData":[TD([[makeQuery(id+"F27.imprint","IMPRINT",EDGE,{"disambiguationData":[TD([[subQ2,-1.0]])],"derivedFrom":subQ1}),1.0]])]});}
            var Q50;
            {var subQ0=sQuery(id+"F27.wireOp",EDGE,"E44.6.0");var subQ1=sQuery(id+"F27.wireOp",EDGE,"E42");var subQ2=makeQuery(id+"F27.imprint","INTERSECT",VERTEX,{"disambiguationData":[OD(0.0)],"derivedFrom":[subQ1,subQ0]});Q50=makeQuery(id+"F27.imprint","IMPRINT",FACE,{"disambiguationData":[TD([[makeQuery(id+"F27.imprint","IMPRINT",EDGE,{"disambiguationData":[TD([[subQ2,-1.0]])],"derivedFrom":subQ1}),-1.0]])]});}
            var Q51;
            {var subQ0=sQuery(id+"F27.wireOp",EDGE,"E44.6.0");var subQ1=sQuery(id+"F27.wireOp",EDGE,"E42");var subQ2=makeQuery(id+"F27.imprint","INTERSECT",VERTEX,{"disambiguationData":[OD(0.0)],"derivedFrom":[subQ1,subQ0]});Q51=makeQuery(id+"F27.imprint","IMPRINT",FACE,{"disambiguationData":[TD([[makeQuery(id+"F27.imprint","IMPRINT",EDGE,{"disambiguationData":[TD([[subQ2,-1.0]])],"derivedFrom":subQ1}),1.0]])]});}
            var Q52;
            {var subQ0=sQuery(id+"F27.wireOp",EDGE,"E44.7.0");var subQ1=sQuery(id+"F27.wireOp",EDGE,"E42");var subQ2=makeQuery(id+"F27.imprint","INTERSECT",VERTEX,{"disambiguationData":[OD(0.0)],"derivedFrom":[subQ1,subQ0]});Q52=makeQuery(id+"F27.imprint","IMPRINT",FACE,{"disambiguationData":[TD([[makeQuery(id+"F27.imprint","IMPRINT",EDGE,{"disambiguationData":[TD([[subQ2,-1.0]])],"derivedFrom":subQ1}),-1.0]])]});}
            var Q53;
            {var subQ0=sQuery(id+"F27.wireOp",EDGE,"E44.7.0");var subQ1=sQuery(id+"F27.wireOp",EDGE,"E42");var subQ2=makeQuery(id+"F27.imprint","INTERSECT",VERTEX,{"disambiguationData":[OD(0.0)],"derivedFrom":[subQ1,subQ0]});Q53=makeQuery(id+"F27.imprint","IMPRINT",FACE,{"disambiguationData":[TD([[makeQuery(id+"F27.imprint","IMPRINT",EDGE,{"disambiguationData":[TD([[subQ2,-1.0]])],"derivedFrom":subQ1}),1.0]])]});}
            var Q54;
            {var subQ0=sQuery(id+"F27.wireOp",EDGE,"E44.8.0");var subQ1=sQuery(id+"F27.wireOp",EDGE,"E42");var subQ2=makeQuery(id+"F27.imprint","INTERSECT",VERTEX,{"disambiguationData":[OD(0.0)],"derivedFrom":[subQ1,subQ0]});Q54=makeQuery(id+"F27.imprint","IMPRINT",FACE,{"disambiguationData":[TD([[makeQuery(id+"F27.imprint","IMPRINT",EDGE,{"disambiguationData":[TD([[subQ2,-1.0]])],"derivedFrom":subQ1}),-1.0]])]});}
            var Q55;
            {var subQ0=sQuery(id+"F27.wireOp",EDGE,"E44.8.0");var subQ1=sQuery(id+"F27.wireOp",EDGE,"E42");var subQ2=makeQuery(id+"F27.imprint","INTERSECT",VERTEX,{"disambiguationData":[OD(0.0)],"derivedFrom":[subQ1,subQ0]});Q55=makeQuery(id+"F27.imprint","IMPRINT",FACE,{"disambiguationData":[TD([[makeQuery(id+"F27.imprint","IMPRINT",EDGE,{"disambiguationData":[TD([[subQ2,-1.0]])],"derivedFrom":subQ1}),1.0]])]});}
            var Q56;
            {var subQ0=sQuery(id+"F27.wireOp",EDGE,"E44.9.0");var subQ1=sQuery(id+"F27.wireOp",EDGE,"E42");var subQ2=makeQuery(id+"F27.imprint","INTERSECT",VERTEX,{"disambiguationData":[OD(0.0)],"derivedFrom":[subQ1,subQ0]});Q56=makeQuery(id+"F27.imprint","IMPRINT",FACE,{"disambiguationData":[TD([[makeQuery(id+"F27.imprint","IMPRINT",EDGE,{"disambiguationData":[TD([[subQ2,-1.0]])],"derivedFrom":subQ1}),-1.0]])]});}
            var Q57;
            {var subQ0=sQuery(id+"F27.wireOp",EDGE,"E44.9.0");var subQ1=sQuery(id+"F27.wireOp",EDGE,"E42");var subQ2=makeQuery(id+"F27.imprint","INTERSECT",VERTEX,{"disambiguationData":[OD(0.0)],"derivedFrom":[subQ1,subQ0]});Q57=makeQuery(id+"F27.imprint","IMPRINT",FACE,{"disambiguationData":[TD([[makeQuery(id+"F27.imprint","IMPRINT",EDGE,{"disambiguationData":[TD([[subQ2,-1.0]])],"derivedFrom":subQ1}),1.0]])]});}
            var Q58;
            {var subQ0=sQuery(id+"F27.wireOp",EDGE,"E44.10.0");var subQ1=sQuery(id+"F27.wireOp",EDGE,"E42");var subQ2=makeQuery(id+"F27.imprint","INTERSECT",VERTEX,{"disambiguationData":[OD(0.0)],"derivedFrom":[subQ1,subQ0]});Q58=makeQuery(id+"F27.imprint","IMPRINT",FACE,{"disambiguationData":[TD([[makeQuery(id+"F27.imprint","IMPRINT",EDGE,{"disambiguationData":[TD([[subQ2,-1.0]])],"derivedFrom":subQ1}),-1.0]])]});}
            var Q59;
            {var subQ0=sQuery(id+"F27.wireOp",EDGE,"E44.10.0");var subQ1=sQuery(id+"F27.wireOp",EDGE,"E42");var subQ2=makeQuery(id+"F27.imprint","INTERSECT",VERTEX,{"disambiguationData":[OD(0.0)],"derivedFrom":[subQ1,subQ0]});Q59=makeQuery(id+"F27.imprint","IMPRINT",FACE,{"disambiguationData":[TD([[makeQuery(id+"F27.imprint","IMPRINT",EDGE,{"disambiguationData":[TD([[subQ2,-1.0]])],"derivedFrom":subQ1}),1.0]])]});}
            var Q60;
            {var subQ0=sQuery(id+"F27.wireOp",EDGE,"E44.11.0");var subQ1=sQuery(id+"F27.wireOp",EDGE,"E42");var subQ2=makeQuery(id+"F27.imprint","INTERSECT",VERTEX,{"disambiguationData":[OD(0.0)],"derivedFrom":[subQ1,subQ0]});Q60=makeQuery(id+"F27.imprint","IMPRINT",FACE,{"disambiguationData":[TD([[makeQuery(id+"F27.imprint","IMPRINT",EDGE,{"disambiguationData":[TD([[subQ2,-1.0]])],"derivedFrom":subQ1}),-1.0]])]});}
            var Q61;
            {var subQ0=sQuery(id+"F27.wireOp",EDGE,"E44.11.0");var subQ1=sQuery(id+"F27.wireOp",EDGE,"E42");var subQ2=makeQuery(id+"F27.imprint","INTERSECT",VERTEX,{"disambiguationData":[OD(0.0)],"derivedFrom":[subQ1,subQ0]});Q61=makeQuery(id+"F27.imprint","IMPRINT",FACE,{"disambiguationData":[TD([[makeQuery(id+"F27.imprint","IMPRINT",EDGE,{"disambiguationData":[TD([[subQ2,-1.0]])],"derivedFrom":subQ1}),1.0]])]});}
            var Q62;
            {var subQ0=sQuery(id+"F27.wireOp",EDGE,"E44.12.0");var subQ1=sQuery(id+"F27.wireOp",EDGE,"E42");var subQ2=makeQuery(id+"F27.imprint","INTERSECT",VERTEX,{"disambiguationData":[OD(0.0)],"derivedFrom":[subQ1,subQ0]});Q62=makeQuery(id+"F27.imprint","IMPRINT",FACE,{"disambiguationData":[TD([[makeQuery(id+"F27.imprint","IMPRINT",EDGE,{"disambiguationData":[TD([[subQ2,-1.0]])],"derivedFrom":subQ1}),-1.0]])]});}
            var Q63;
            {var subQ0=sQuery(id+"F27.wireOp",EDGE,"E44.12.0");var subQ1=sQuery(id+"F27.wireOp",EDGE,"E42");var subQ2=makeQuery(id+"F27.imprint","INTERSECT",VERTEX,{"disambiguationData":[OD(0.0)],"derivedFrom":[subQ1,subQ0]});Q63=makeQuery(id+"F27.imprint","IMPRINT",FACE,{"disambiguationData":[TD([[makeQuery(id+"F27.imprint","IMPRINT",EDGE,{"disambiguationData":[TD([[subQ2,-1.0]])],"derivedFrom":subQ1}),1.0]])]});}
            var Q64;
            {var subQ0=sQuery(id+"F27.wireOp",EDGE,"E44.13.0");var subQ1=sQuery(id+"F27.wireOp",EDGE,"E42");var subQ2=makeQuery(id+"F27.imprint","INTERSECT",VERTEX,{"disambiguationData":[OD(0.0)],"derivedFrom":[subQ1,subQ0]});Q64=makeQuery(id+"F27.imprint","IMPRINT",FACE,{"disambiguationData":[TD([[makeQuery(id+"F27.imprint","IMPRINT",EDGE,{"disambiguationData":[TD([[subQ2,-1.0]])],"derivedFrom":subQ1}),-1.0]])]});}
            var Q65;
            {var subQ0=sQuery(id+"F27.wireOp",EDGE,"E44.13.0");var subQ1=sQuery(id+"F27.wireOp",EDGE,"E42");var subQ2=makeQuery(id+"F27.imprint","INTERSECT",VERTEX,{"disambiguationData":[OD(0.0)],"derivedFrom":[subQ1,subQ0]});Q65=makeQuery(id+"F27.imprint","IMPRINT",FACE,{"disambiguationData":[TD([[makeQuery(id+"F27.imprint","IMPRINT",EDGE,{"disambiguationData":[TD([[subQ2,-1.0]])],"derivedFrom":subQ1}),1.0]])]});}
            var Q66;
            {var subQ0=sQuery(id+"F27.wireOp",EDGE,"E44.14.0");var subQ1=sQuery(id+"F27.wireOp",EDGE,"E42");var subQ2=makeQuery(id+"F27.imprint","INTERSECT",VERTEX,{"disambiguationData":[OD(0.0)],"derivedFrom":[subQ1,subQ0]});Q66=makeQuery(id+"F27.imprint","IMPRINT",FACE,{"disambiguationData":[TD([[makeQuery(id+"F27.imprint","IMPRINT",EDGE,{"disambiguationData":[TD([[subQ2,-1.0]])],"derivedFrom":subQ1}),-1.0]])]});}
            var Q67;
            {var subQ0=sQuery(id+"F27.wireOp",EDGE,"E44.14.0");var subQ1=sQuery(id+"F27.wireOp",EDGE,"E42");var subQ2=makeQuery(id+"F27.imprint","INTERSECT",VERTEX,{"disambiguationData":[OD(0.0)],"derivedFrom":[subQ1,subQ0]});Q67=makeQuery(id+"F27.imprint","IMPRINT",FACE,{"disambiguationData":[TD([[makeQuery(id+"F27.imprint","IMPRINT",EDGE,{"disambiguationData":[TD([[subQ2,-1.0]])],"derivedFrom":subQ1}),1.0]])]});}
            var Q68;
            {var subQ0=sQuery(id+"F27.wireOp",EDGE,"E44.15.0");var subQ1=sQuery(id+"F27.wireOp",EDGE,"E42");var subQ2=makeQuery(id+"F27.imprint","INTERSECT",VERTEX,{"disambiguationData":[OD(0.0)],"derivedFrom":[subQ1,subQ0]});Q68=makeQuery(id+"F27.imprint","IMPRINT",FACE,{"disambiguationData":[TD([[makeQuery(id+"F27.imprint","IMPRINT",EDGE,{"disambiguationData":[TD([[subQ2,-1.0]])],"derivedFrom":subQ1}),-1.0]])]});}
            var Q69;
            {var subQ0=sQuery(id+"F27.wireOp",EDGE,"E44.15.0");var subQ1=sQuery(id+"F27.wireOp",EDGE,"E42");var subQ2=makeQuery(id+"F27.imprint","INTERSECT",VERTEX,{"disambiguationData":[OD(0.0)],"derivedFrom":[subQ1,subQ0]});Q69=makeQuery(id+"F27.imprint","IMPRINT",FACE,{"disambiguationData":[TD([[makeQuery(id+"F27.imprint","IMPRINT",EDGE,{"disambiguationData":[TD([[subQ2,-1.0]])],"derivedFrom":subQ1}),1.0]])]});}
            var Q70;
            {var subQ0=sQuery(id+"F27.wireOp",EDGE,"E44.16.0");var subQ1=sQuery(id+"F27.wireOp",EDGE,"E42");var subQ2=makeQuery(id+"F27.imprint","INTERSECT",VERTEX,{"disambiguationData":[OD(0.0)],"derivedFrom":[subQ1,subQ0]});Q70=makeQuery(id+"F27.imprint","IMPRINT",FACE,{"disambiguationData":[TD([[makeQuery(id+"F27.imprint","IMPRINT",EDGE,{"disambiguationData":[TD([[subQ2,-1.0]])],"derivedFrom":subQ1}),-1.0]])]});}
            var Q71;
            {var subQ0=sQuery(id+"F27.wireOp",EDGE,"E44.16.0");var subQ1=sQuery(id+"F27.wireOp",EDGE,"E42");var subQ2=makeQuery(id+"F27.imprint","INTERSECT",VERTEX,{"disambiguationData":[OD(0.0)],"derivedFrom":[subQ1,subQ0]});Q71=makeQuery(id+"F27.imprint","IMPRINT",FACE,{"disambiguationData":[TD([[makeQuery(id+"F27.imprint","IMPRINT",EDGE,{"disambiguationData":[TD([[subQ2,-1.0]])],"derivedFrom":subQ1}),1.0]])]});}
            var Q72;
            {var subQ0=sQuery(id+"F27.wireOp",EDGE,"E44.17.0");var subQ1=sQuery(id+"F27.wireOp",EDGE,"E42");var subQ2=makeQuery(id+"F27.imprint","INTERSECT",VERTEX,{"disambiguationData":[OD(0.0)],"derivedFrom":[subQ1,subQ0]});Q72=makeQuery(id+"F27.imprint","IMPRINT",FACE,{"disambiguationData":[TD([[makeQuery(id+"F27.imprint","IMPRINT",EDGE,{"disambiguationData":[TD([[subQ2,-1.0]])],"derivedFrom":subQ1}),-1.0]])]});}
            var Q73;
            {var subQ0=sQuery(id+"F27.wireOp",EDGE,"E44.17.0");var subQ1=sQuery(id+"F27.wireOp",EDGE,"E42");var subQ2=makeQuery(id+"F27.imprint","INTERSECT",VERTEX,{"disambiguationData":[OD(0.0)],"derivedFrom":[subQ1,subQ0]});Q73=makeQuery(id+"F27.imprint","IMPRINT",FACE,{"disambiguationData":[TD([[makeQuery(id+"F27.imprint","IMPRINT",EDGE,{"disambiguationData":[TD([[subQ2,-1.0]])],"derivedFrom":subQ1}),1.0]])]});}
            var Q74;
            {var subQ0=sQuery(id+"F27.wireOp",EDGE,"E44.18.0");var subQ1=sQuery(id+"F27.wireOp",EDGE,"E42");var subQ2=makeQuery(id+"F27.imprint","INTERSECT",VERTEX,{"disambiguationData":[OD(0.0)],"derivedFrom":[subQ1,subQ0]});Q74=makeQuery(id+"F27.imprint","IMPRINT",FACE,{"disambiguationData":[TD([[makeQuery(id+"F27.imprint","IMPRINT",EDGE,{"disambiguationData":[TD([[subQ2,-1.0]])],"derivedFrom":subQ1}),-1.0]])]});}
            var Q75;
            {var subQ0=sQuery(id+"F27.wireOp",EDGE,"E44.18.0");var subQ1=sQuery(id+"F27.wireOp",EDGE,"E42");var subQ2=makeQuery(id+"F27.imprint","INTERSECT",VERTEX,{"disambiguationData":[OD(0.0)],"derivedFrom":[subQ1,subQ0]});Q75=makeQuery(id+"F27.imprint","IMPRINT",FACE,{"disambiguationData":[TD([[makeQuery(id+"F27.imprint","IMPRINT",EDGE,{"disambiguationData":[TD([[subQ2,-1.0]])],"derivedFrom":subQ1}),1.0]])]});}
            var Q76;
            {var subQ0=sQuery(id+"F27.wireOp",EDGE,"E44.19.0");var subQ1=sQuery(id+"F27.wireOp",EDGE,"E42");var subQ2=makeQuery(id+"F27.imprint","INTERSECT",VERTEX,{"disambiguationData":[OD(0.0)],"derivedFrom":[subQ1,subQ0]});Q76=makeQuery(id+"F27.imprint","IMPRINT",FACE,{"disambiguationData":[TD([[makeQuery(id+"F27.imprint","IMPRINT",EDGE,{"disambiguationData":[TD([[subQ2,-1.0]])],"derivedFrom":subQ1}),-1.0]])]});}
            var Q77;
            {var subQ0=sQuery(id+"F27.wireOp",EDGE,"E44.19.0");var subQ1=sQuery(id+"F27.wireOp",EDGE,"E42");var subQ2=makeQuery(id+"F27.imprint","INTERSECT",VERTEX,{"disambiguationData":[OD(0.0)],"derivedFrom":[subQ1,subQ0]});Q77=makeQuery(id+"F27.imprint","IMPRINT",FACE,{"disambiguationData":[TD([[makeQuery(id+"F27.imprint","IMPRINT",EDGE,{"disambiguationData":[TD([[subQ2,-1.0]])],"derivedFrom":subQ1}),1.0]])]});}
            var Q78;
            {var subQ0=sQuery(id+"F27.wireOp",EDGE,"E45.1.20.0");var subQ1=sQuery(id+"F27.wireOp",EDGE,"E42");var subQ2=makeQuery(id+"F27.imprint","INTERSECT",VERTEX,{"disambiguationData":[OD(0.0)],"derivedFrom":[subQ1,subQ0]});Q78=makeQuery(id+"F27.imprint","IMPRINT",FACE,{"disambiguationData":[TD([[makeQuery(id+"F27.imprint","IMPRINT",EDGE,{"disambiguationData":[TD([[subQ2,1.0]])],"derivedFrom":subQ1}),-1.0]])]});}
            var Q79;
            {var subQ0=sQuery(id+"F27.wireOp",EDGE,"E45.1.20.0");var subQ1=sQuery(id+"F27.wireOp",EDGE,"E42");var subQ2=makeQuery(id+"F27.imprint","INTERSECT",VERTEX,{"disambiguationData":[OD(0.0)],"derivedFrom":[subQ1,subQ0]});Q79=makeQuery(id+"F27.imprint","IMPRINT",FACE,{"disambiguationData":[TD([[makeQuery(id+"F27.imprint","IMPRINT",EDGE,{"disambiguationData":[TD([[subQ2,1.0]])],"derivedFrom":subQ1}),1.0]])]});}
            extrude(context, id + "F28", {"entities" : qUnion([Q0, Q1, Q2, Q3, Q4, Q5, Q6, Q7, Q8, Q9, Q10, Q11, Q12, Q13, Q14, Q15, Q16, Q17, Q18, Q19, Q20, Q21, Q22, Q23, Q24, Q25, Q26, Q27, Q28, Q29, Q30, Q31, Q32, Q33, Q34, Q35, Q36, Q37, Q38, Q39, Q40, Q41, Q42, Q43, Q44, Q45, Q46, Q47, Q48, Q49, Q50, Q51, Q52, Q53, Q54, Q55, Q56, Q57, Q58, Q59, Q60, Q61, Q62, Q63, Q64, Q65, Q66, Q67, Q68, Q69, Q70, Q71, Q72, Q73, Q74, Q75, Q76, Q77, Q78, Q79]), "operationType" : NewBodyOperationType.ADD, "oppositeDirection" : true, "depth" : 12 * mm});
        }
        {
            var Q0;
            Q0=makeQuery(id+"F12.opExtrude","CAP_FACE",FACE,{"disambiguationData":[OSD([sQuery(id+"F6.wireOp",EDGE,"E8.3.0.1"),sQuery(id+"F11.wireOp",EDGE,"E10")])],"isStart":false});
            var sketch = newSketch(context, id + "F29", { "sketchPlane" : qUnion([Q0])});
            skLineSegment(sketch, "E47.bottom", {"start": v(66.5, -40.63) * mm, "end": v(58.5, -40.63) * mm});
            skLineSegment(sketch, "E47.top", {"start": v(66.5, -26.13) * mm, "end": v(58.5, -26.13) * mm});
            skLineSegment(sketch, "E47.left", {"start": v(66.5, -40.63) * mm, "end": v(66.5, -26.13) * mm});
            skLineSegment(sketch, "E47.right", {"start": v(58.5, -40.63) * mm, "end": v(58.5, -26.13) * mm});
            skLineSegment(sketch, "E48", {"start": v(66.5, -37.13) * mm, "end": v(58.5, -37.13) * mm});
            skLineSegment(sketch, "E49", {"start": v(62.5, -37.13) * mm, "end": v(62.5, -39.63) * mm});
            skArc(sketch, "E50", {"start": v(65, -39.63) * mm, "mid": v(62.5, -37.13) * mm, "end": v(60, -39.63) * mm});
            skLineSegment(sketch, "E51", {"start": v(65, -39.63) * mm, "end": v(65, -40.63) * mm});
            skLineSegment(sketch, "E52", {"start": v(60, -39.63) * mm, "end": v(60, -40.63) * mm});
            skSolve(sketch);
        }
        {
            var Q0;
            {var subQ1=sQuery(id+"F29.wireOp",EDGE,"E47.top");Q0=makeQuery(id+"F29.imprint","IMPRINT",FACE,{"disambiguationData":[TD([[makeQuery(id+"F29.imprint","IMPRINT",EDGE,{"derivedFrom":subQ1}),1.0]])]});}
            var Q1;
            {var subQ7=sQuery(id+"F29.wireOp",EDGE,"E51");Q1=makeQuery(id+"F29.imprint","IMPRINT",FACE,{"disambiguationData":[TD([[makeQuery(id+"F29.imprint","IMPRINT",EDGE,{"derivedFrom":subQ7}),1.0]])]});}
            var Q2;
            {var subQ5=sQuery(id+"F29.wireOp",EDGE,"E52");Q2=makeQuery(id+"F29.imprint","IMPRINT",FACE,{"disambiguationData":[TD([[makeQuery(id+"F29.imprint","IMPRINT",EDGE,{"derivedFrom":subQ5}),-1.0]])]});}
            var Q3;
            Q3=sQuery(id+"F29.wireOp",EDGE,"E47.top");
            revolve(context, id + "F30", {"entities" : qUnion([Q0, Q1, Q2]), "axis" : qUnion([Q3]), "revolveType" : RevolveType.FULL});
        }
        {
            var Q0;
            Q0=makeQuery(id+"F30.opRevolve","SWEPT_FACE",FACE,{"disambiguationData":[OSD([sQuery(id+"F29.wireOp",EDGE,"E47.left")])]});
            var sketch = newSketch(context, id + "F31", { "sketchPlane" : qUnion([Q0])});
            skCircle(sketch, "E53", {"center": v(26.13, -21.5) * mm, "radius": 3 * mm});
            skCircle(sketch, "E54", {"center": v(26.13, -21.5) * mm, "radius": 9 * mm});
            skSolve(sketch);
        }
        {
            var Q0;
            Q0=makeQuery(id+"F31.imprint","IMPRINT",FACE,{"disambiguationData":[TD([[makeQuery(id+"F31.imprint","IMPRINT",EDGE,{"derivedFrom":sQuery(id+"F31.wireOp",EDGE,"E53")}),1.0]])]});
            extrude(context, id + "F32", {"entities" : qUnion([Q0]), "operationType" : NewBodyOperationType.REMOVE, "oppositeDirection" : true, "depth" : 8 * mm});
        }
        {
            var Q0;
            Q0=makeQuery(id+"F31.imprint","IMPRINT",FACE,{"disambiguationData":[TD([[makeQuery(id+"F31.imprint","IMPRINT",EDGE,{"derivedFrom":sQuery(id+"F31.wireOp",EDGE,"E53")}),-1.0]])]});
            extrude(context, id + "F33", {"entities" : qUnion([Q0]), "operationType" : NewBodyOperationType.REMOVE, "oppositeDirection" : true, "depth" : 0.5 * mm});
        }
        {
            var Q0;
            Q0=makeQuery(id+"F30.opRevolve","SWEPT_FACE",FACE,{"disambiguationData":[OSD([sQuery(id+"F29.wireOp",EDGE,"E47.right")])]});
            var sketch = newSketch(context, id + "F34", { "sketchPlane" : qUnion([Q0])});
            skCircle(sketch, "E55", {"center": v(-26.13, -21.5) * mm, "radius": 9 * mm});
            skSolve(sketch);
        }
        {
            var Q0;
            Q0=makeQuery(id+"F34.imprint","IMPRINT",FACE,{"disambiguationData":[TD([[makeQuery(id+"F34.imprint","IMPRINT",EDGE,{"derivedFrom":sQuery(id+"F34.wireOp",EDGE,"E55")}),1.0]])]});
            extrude(context, id + "F35", {"entities" : qUnion([Q0]), "operationType" : NewBodyOperationType.REMOVE, "oppositeDirection" : true, "depth" : 0.5 * mm});
        }
        {
            var Q0;
            Q0=makeQuery(id+"F15.opExtrude","CAP_EDGE",EDGE,{"disambiguationData":[OSD([sQuery(id+"F14.wireOp",EDGE,"E18"),sQuery(id+"F14.wireOp",EDGE,"E19")])],"isStart":false});
            var Q1;
            Q1=makeQuery(id+"F15.opExtrude","CAP_EDGE",EDGE,{"disambiguationData":[OSD([sQuery(id+"F14.wireOp",EDGE,"E17")])],"isStart":false});
            var Q2;
            Q2=makeQuery(id+"F15.opExtrude","CAP_EDGE",EDGE,{"disambiguationData":[OSD([sQuery(id+"F14.wireOp",EDGE,"E13")])],"isStart":false});
            var Q3;
            Q3=makeQuery(id+"F15.opExtrude","CAP_EDGE",EDGE,{"disambiguationData":[OSD([sQuery(id+"F14.wireOp",EDGE,"E12")])],"isStart":false});
            var Q4;
            {var subQ0=sQuery(id+"F14.wireOp",EDGE,"E15");var subQ1=sQuery(id+"F14.wireOp",EDGE,"E12");Q4=makeQuery(id+"F16.opFillet","BLEND_EDGE",EDGE,{"blendedFrom":[makeQuery(id+"F15.opExtrude","SWEPT_EDGE",EDGE,{"disambiguationData":[OSD([subQ1,subQ0])]}),makeQuery(id+"F15.opExtrude","CAP_FACE",FACE,{"disambiguationData":[OSD([sQuery(id+"F14.wireOp",EDGE,"E11.bottom"),sQuery(id+"F14.wireOp",EDGE,"E11.top"),sQuery(id+"F14.wireOp",EDGE,"E11.left"),sQuery(id+"F14.wireOp",EDGE,"E11.right"),subQ1,sQuery(id+"F14.wireOp",EDGE,"E13"),subQ0,sQuery(id+"F14.wireOp",EDGE,"E16"),sQuery(id+"F14.wireOp",EDGE,"E17"),sQuery(id+"F14.wireOp",EDGE,"E18"),sQuery(id+"F14.wireOp",EDGE,"E19"),sQuery(id+"F14.wireOp",EDGE,"E20"),sQuery(id+"F14.wireOp",EDGE,"E21")])],"isStart":false})],"blendedInto":[makeQuery(id+"F15.opExtrude","CAP_FACE",FACE,{"disambiguationData":[OSD([sQuery(id+"F14.wireOp",EDGE,"E11.bottom"),sQuery(id+"F14.wireOp",EDGE,"E11.top"),sQuery(id+"F14.wireOp",EDGE,"E11.left"),sQuery(id+"F14.wireOp",EDGE,"E11.right"),subQ1,sQuery(id+"F14.wireOp",EDGE,"E13"),subQ0,sQuery(id+"F14.wireOp",EDGE,"E16"),sQuery(id+"F14.wireOp",EDGE,"E17"),sQuery(id+"F14.wireOp",EDGE,"E18"),sQuery(id+"F14.wireOp",EDGE,"E19"),sQuery(id+"F14.wireOp",EDGE,"E20"),sQuery(id+"F14.wireOp",EDGE,"E21")])],"isStart":false})]});}
            var Q5;
            Q5=makeQuery(id+"F15.opExtrude","CAP_EDGE",EDGE,{"disambiguationData":[OSD([sQuery(id+"F14.wireOp",EDGE,"E15")])],"isStart":false});
            var Q6;
            Q6=makeQuery(id+"F15.opExtrude","CAP_EDGE",EDGE,{"disambiguationData":[OSD([sQuery(id+"F14.wireOp",EDGE,"E20")])],"isStart":false});
            var Q7;
            Q7=makeQuery(id+"F15.opExtrude","SWEPT_EDGE",EDGE,{"disambiguationData":[OSD([sQuery(id+"F14.wireOp",EDGE,"E20"),sQuery(id+"F14.wireOp",EDGE,"E21")])]});
            var Q8;
            Q8=makeQuery(id+"F15.opExtrude","SWEPT_EDGE",EDGE,{"disambiguationData":[OSD([sQuery(id+"F14.wireOp",EDGE,"E19"),sQuery(id+"F14.wireOp",EDGE,"E20")])]});
            var Q9;
            Q9=makeQuery(id+"F15.opExtrude","CAP_EDGE",EDGE,{"disambiguationData":[OSD([sQuery(id+"F14.wireOp",EDGE,"E15")])],"isStart":true});
            var Q10;
            Q10=makeQuery(id+"F15.opExtrude","CAP_EDGE",EDGE,{"disambiguationData":[OSD([sQuery(id+"F14.wireOp",EDGE,"E21")])],"isStart":true});
            var Q11;
            Q11=makeQuery(id+"F15.opExtrude","CAP_EDGE",EDGE,{"disambiguationData":[OSD([sQuery(id+"F14.wireOp",EDGE,"E20")])],"isStart":true});
            var Q12;
            Q12=makeQuery(id+"F15.opExtrude","CAP_EDGE",EDGE,{"disambiguationData":[OSD([sQuery(id+"F14.wireOp",EDGE,"E18"),sQuery(id+"F14.wireOp",EDGE,"E19")])],"isStart":true});
            var Q13;
            Q13=makeQuery(id+"F15.opExtrude","CAP_EDGE",EDGE,{"disambiguationData":[OSD([sQuery(id+"F14.wireOp",EDGE,"E17")])],"isStart":true});
            var Q14;
            Q14=makeQuery(id+"F15.opExtrude","SWEPT_EDGE",EDGE,{"disambiguationData":[OSD([sQuery(id+"F14.wireOp",EDGE,"E12"),sQuery(id+"F14.wireOp",EDGE,"E13")])]});
            var Q15;
            Q15=makeQuery(id+"F15.opExtrude","SWEPT_EDGE",EDGE,{"disambiguationData":[OSD([sQuery(id+"F14.wireOp",EDGE,"E13"),sQuery(id+"F14.wireOp",EDGE,"E17")])]});
            var Q16;
            Q16=makeQuery(id+"F15.opExtrude","CAP_EDGE",EDGE,{"disambiguationData":[OSD([sQuery(id+"F14.wireOp",EDGE,"E13")])],"isStart":true});
            fillet(context, id + "F36", {"entities" : qUnion([Q0, Q1, Q2, Q3, Q4, Q5, Q6, Q7, Q8, Q9, Q10, Q11, Q12, Q13, Q14, Q15, Q16]), "radius" : 3 * mm, "tangentPropagation" : true, "allowEdgeOverflow" : false});
        }
        {
            var Q0;
            Q0=makeQuery(id+"F15.opExtrude","SWEPT_EDGE",EDGE,{"disambiguationData":[OSD([sQuery(id+"F14.wireOp",EDGE,"E17"),sQuery(id+"F14.wireOp",EDGE,"E18")])]});
            fillet(context, id + "F37", {"entities" : qUnion([Q0]), "radius" : 10 * mm, "tangentPropagation" : true, "allowEdgeOverflow" : false});
        }
        {
            var Q0;
            Q0=makeQuery(id+"F19.imprint","IMPRINT",FACE,{"disambiguationData":[TD([[makeQuery(id+"F19.imprint","IMPRINT",EDGE,{"derivedFrom":sQuery(id+"F19.wireOp",EDGE,"E33")}),-1.0]])]});
            extrude(context, id + "F38", {"entities" : qUnion([Q0]), "operationType" : NewBodyOperationType.ADD, "depth" : 26 * mm});
        }
        {
            var Q0;
            Q0=makeQuery(id+"F19.imprint","IMPRINT",FACE,{"disambiguationData":[TD([[makeQuery(id+"F19.imprint","IMPRINT",EDGE,{"derivedFrom":sQuery(id+"F19.wireOp",EDGE,"E33")}),1.0]])]});
            extrude(context, id + "F39", {"entities" : qUnion([Q0]), "operationType" : NewBodyOperationType.ADD, "depth" : 46 * mm});
        }
    });
